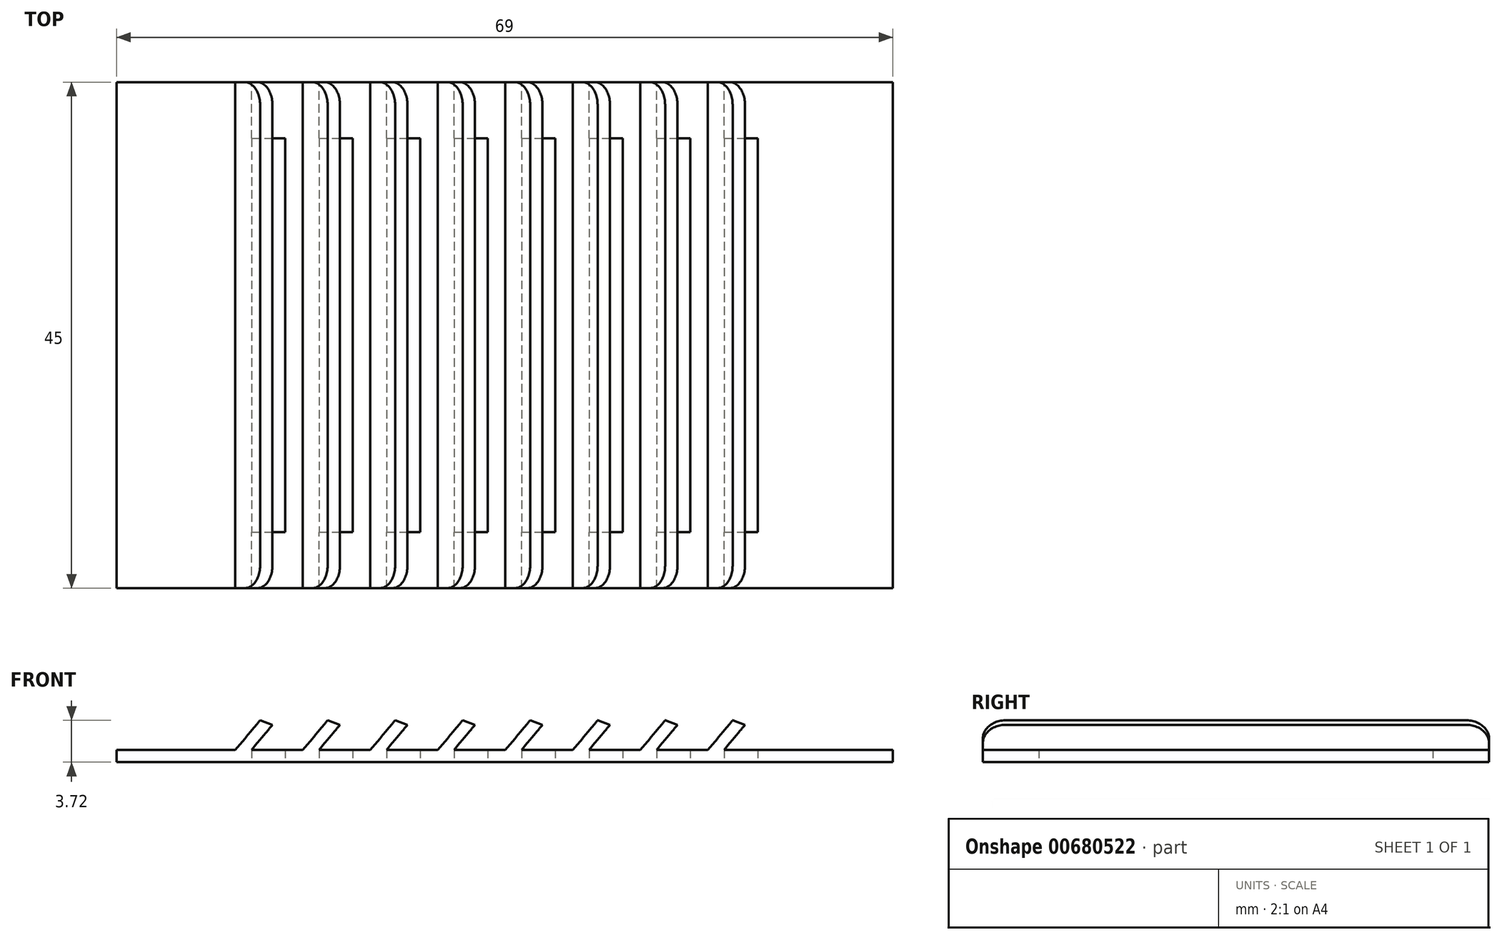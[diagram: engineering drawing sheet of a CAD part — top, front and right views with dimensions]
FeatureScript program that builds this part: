
annotation { "Feature Type Name" : "Feature", "Feature Type Description" : "" }
export const myFeature = defineFeature(function(context is Context, id is Id, definition is map)
    precondition{}
    {
        {
            var Q0;
            Q0=qCreatedBy(makeId("Top.planeOp"),FACE);
            var sketch = newSketch(context, id + "F0", { "sketchPlane" : qUnion([Q0])});
            skLineSegment(sketch, "E0.bottom", {"start": v(0, 0) * mm, "end": v(69, 0) * mm});
            skLineSegment(sketch, "E0.top", {"start": v(0, -45) * mm, "end": v(69, -45) * mm});
            skLineSegment(sketch, "E0.left", {"start": v(0, 0) * mm, "end": v(0, -45) * mm});
            skLineSegment(sketch, "E0.right", {"start": v(69, 0) * mm, "end": v(69, -45) * mm});
            skLineSegment(sketch, "E1.bottom", {"start": v(12, -5) * mm, "end": v(15, -5) * mm});
            skLineSegment(sketch, "E1.top", {"start": v(12, -40) * mm, "end": v(15, -40) * mm});
            skLineSegment(sketch, "E1.left", {"start": v(12, -5) * mm, "end": v(12, -40) * mm});
            skLineSegment(sketch, "E1.right", {"start": v(15, -5) * mm, "end": v(15, -40) * mm});
            skLineSegment(sketch, "E2.1.0.0", {"start": v(18, -40) * mm, "end": v(21, -40) * mm});
            skLineSegment(sketch, "E2.1.0.1", {"start": v(18, -5) * mm, "end": v(21, -5) * mm});
            skLineSegment(sketch, "E2.1.0.2", {"start": v(18, -5) * mm, "end": v(18, -40) * mm});
            skLineSegment(sketch, "E2.1.0.3", {"start": v(21, -5) * mm, "end": v(21, -40) * mm});
            skLineSegment(sketch, "E2.2.0.0", {"start": v(24, -40) * mm, "end": v(27, -40) * mm});
            skLineSegment(sketch, "E2.2.0.1", {"start": v(24, -5) * mm, "end": v(27, -5) * mm});
            skLineSegment(sketch, "E2.2.0.2", {"start": v(24, -5) * mm, "end": v(24, -40) * mm});
            skLineSegment(sketch, "E2.2.0.3", {"start": v(27, -5) * mm, "end": v(27, -40) * mm});
            skLineSegment(sketch, "E2.direction1", {"start": v(12, -40) * mm, "end": v(18, -40) * mm, "construction": true});
            skLineSegment(sketch, "E3.0.3.0", {"start": v(30, -40) * mm, "end": v(33, -40) * mm});
            skLineSegment(sketch, "E3.3.3.0", {"start": v(30, -5) * mm, "end": v(33, -5) * mm});
            skLineSegment(sketch, "E3.6.3.0", {"start": v(30, -5) * mm, "end": v(30, -40) * mm});
            skLineSegment(sketch, "E3.9.3.0", {"start": v(33, -5) * mm, "end": v(33, -40) * mm});
            skLineSegment(sketch, "E3.0.4.0", {"start": v(36, -40) * mm, "end": v(39, -40) * mm});
            skLineSegment(sketch, "E3.3.4.0", {"start": v(36, -5) * mm, "end": v(39, -5) * mm});
            skLineSegment(sketch, "E3.6.4.0", {"start": v(36, -5) * mm, "end": v(36, -40) * mm});
            skLineSegment(sketch, "E3.9.4.0", {"start": v(39, -5) * mm, "end": v(39, -40) * mm});
            skLineSegment(sketch, "E3.0.5.0", {"start": v(42, -40) * mm, "end": v(45, -40) * mm});
            skLineSegment(sketch, "E3.3.5.0", {"start": v(42, -5) * mm, "end": v(45, -5) * mm});
            skLineSegment(sketch, "E3.6.5.0", {"start": v(42, -5) * mm, "end": v(42, -40) * mm});
            skLineSegment(sketch, "E3.9.5.0", {"start": v(45, -5) * mm, "end": v(45, -40) * mm});
            skLineSegment(sketch, "E4.0.6.0", {"start": v(48, -40) * mm, "end": v(51, -40) * mm});
            skLineSegment(sketch, "E4.3.6.0", {"start": v(48, -5) * mm, "end": v(51, -5) * mm});
            skLineSegment(sketch, "E4.6.6.0", {"start": v(48, -5) * mm, "end": v(48, -40) * mm});
            skLineSegment(sketch, "E4.9.6.0", {"start": v(51, -5) * mm, "end": v(51, -40) * mm});
            skLineSegment(sketch, "E4.0.7.0", {"start": v(54, -40) * mm, "end": v(57, -40) * mm});
            skLineSegment(sketch, "E4.3.7.0", {"start": v(54, -5) * mm, "end": v(57, -5) * mm});
            skLineSegment(sketch, "E4.6.7.0", {"start": v(54, -5) * mm, "end": v(54, -40) * mm});
            skLineSegment(sketch, "E4.9.7.0", {"start": v(57, -5) * mm, "end": v(57, -40) * mm});
            skSolve(sketch);
        }
        {
            var Q0;
            Q0=makeQuery(id+"F0.imprint","IMPRINT",FACE,{"disambiguationData":[TD([[makeQuery(id+"F0.imprint","IMPRINT",EDGE,{"derivedFrom":sQuery(id+"F0.wireOp",EDGE,"E0.bottom")}),-1.0]])]});
            extrude(context, id + "F1", {"entities" : qUnion([Q0]), "depth" : 1.1 * mm, "offsetDistance" : 25 * mm});
        }
        {
            var Q0;
            Q0=makeQuery(id+"F1.opExtrude","SWEPT_FACE",FACE,{"disambiguationData":[OSD([sQuery(id+"F0.wireOp",EDGE,"E0.bottom")])]});
            var sketch = newSketch(context, id + "F2", { "sketchPlane" : qUnion([Q0])});
            skLineSegment(sketch, "E5.0.0", {"start": v(0, 0) * mm, "end": v(-69, 0) * mm, "construction": true});
            skLineSegment(sketch, "E5.0.1", {"start": v(-69, 0) * mm, "end": v(-69, 1.1) * mm, "construction": true});
            skLineSegment(sketch, "E5.0.2", {"start": v(-69, 1.1) * mm, "end": v(0, 1.1) * mm});
            skLineSegment(sketch, "E5.0.3", {"start": v(0, 1.1) * mm, "end": v(0, 0) * mm, "construction": true});
            skLineSegment(sketch, "E6.0.0", {"start": v(-12, 0) * mm, "end": v(-15, 0) * mm, "construction": true});
            skLineSegment(sketch, "E6.0.1", {"start": v(-15, 0) * mm, "end": v(-15, 1.1) * mm, "construction": true});
            skLineSegment(sketch, "E6.0.2", {"start": v(-15, 1.1) * mm, "end": v(-12, 1.1) * mm, "construction": true});
            skLineSegment(sketch, "E6.0.3", {"start": v(-12, 1.1) * mm, "end": v(-12, 0) * mm, "construction": true});
            skLineSegment(sketch, "E7.0.0", {"start": v(-54, 0) * mm, "end": v(-57, 0) * mm, "construction": true});
            skLineSegment(sketch, "E7.0.1", {"start": v(-57, 0) * mm, "end": v(-57, 1.1) * mm, "construction": true});
            skLineSegment(sketch, "E7.0.2", {"start": v(-57, 1.1) * mm, "end": v(-54, 1.1) * mm, "construction": true});
            skLineSegment(sketch, "E7.0.3", {"start": v(-54, 1.1) * mm, "end": v(-54, 0) * mm, "construction": true});
            skLineSegment(sketch, "E8", {"start": v(-12, 1.1) * mm, "end": v(-14, 3.48) * mm});
            skLineSegment(sketch, "E9", {"start": v(-14, 3.48) * mm, "end": v(-14, 5.2) * mm});
            skLineSegment(sketch, "E10", {"start": v(-14, 5.2) * mm, "end": v(-10.56, 1.1) * mm});
            skLineSegment(sketch, "E11.1.0.0", {"start": v(-20, 3.48) * mm, "end": v(-20, 5.2) * mm});
            skLineSegment(sketch, "E11.1.0.1", {"start": v(-18, 1.1) * mm, "end": v(-20, 3.48) * mm});
            skLineSegment(sketch, "E11.1.0.2", {"start": v(-20, 5.2) * mm, "end": v(-16.56, 1.1) * mm});
            skLineSegment(sketch, "E11.2.0.0", {"start": v(-26, 3.48) * mm, "end": v(-26, 5.2) * mm});
            skLineSegment(sketch, "E11.2.0.1", {"start": v(-24, 1.1) * mm, "end": v(-26, 3.48) * mm});
            skLineSegment(sketch, "E11.2.0.2", {"start": v(-26, 5.2) * mm, "end": v(-22.56, 1.1) * mm});
            skLineSegment(sketch, "E11.3.0.0", {"start": v(-32, 3.48) * mm, "end": v(-32, 5.2) * mm});
            skLineSegment(sketch, "E11.3.0.1", {"start": v(-30, 1.1) * mm, "end": v(-32, 3.48) * mm});
            skLineSegment(sketch, "E11.3.0.2", {"start": v(-32, 5.2) * mm, "end": v(-28.56, 1.1) * mm});
            skLineSegment(sketch, "E11.4.0.0", {"start": v(-38, 3.48) * mm, "end": v(-38, 5.2) * mm});
            skLineSegment(sketch, "E11.4.0.1", {"start": v(-36, 1.1) * mm, "end": v(-38, 3.48) * mm});
            skLineSegment(sketch, "E11.4.0.2", {"start": v(-38, 5.2) * mm, "end": v(-34.56, 1.1) * mm});
            skLineSegment(sketch, "E11.5.0.0", {"start": v(-44, 3.48) * mm, "end": v(-44, 5.2) * mm});
            skLineSegment(sketch, "E11.5.0.1", {"start": v(-42, 1.1) * mm, "end": v(-44, 3.48) * mm});
            skLineSegment(sketch, "E11.5.0.2", {"start": v(-44, 5.2) * mm, "end": v(-40.56, 1.1) * mm});
            skLineSegment(sketch, "E11.6.0.0", {"start": v(-50, 3.48) * mm, "end": v(-50, 5.2) * mm});
            skLineSegment(sketch, "E11.6.0.1", {"start": v(-48, 1.1) * mm, "end": v(-50, 3.48) * mm});
            skLineSegment(sketch, "E11.6.0.2", {"start": v(-50, 5.2) * mm, "end": v(-46.56, 1.1) * mm});
            skLineSegment(sketch, "E11.7.0.0", {"start": v(-56, 3.48) * mm, "end": v(-56, 5.2) * mm});
            skLineSegment(sketch, "E11.7.0.1", {"start": v(-54, 1.1) * mm, "end": v(-56, 3.48) * mm});
            skLineSegment(sketch, "E11.7.0.2", {"start": v(-56, 5.2) * mm, "end": v(-52.56, 1.1) * mm});
            skLineSegment(sketch, "E11.direction1", {"start": v(-14, 3.48) * mm, "end": v(-20, 3.48) * mm, "construction": true});
            skSolve(sketch);
        }
        {
            var Q0;
            {var subQ0=sQuery(id+"F2.wireOp",EDGE,"E8");Q0=makeQuery(id+"F2.imprint","IMPRINT",FACE,{"disambiguationData":[TD([[makeQuery(id+"F2.imprint","IMPRINT",EDGE,{"derivedFrom":subQ0}),-1.0]])]});}
            var Q1;
            Q1=makeQuery(id+"F2.imprint","IMPRINT",FACE,{"disambiguationData":[TD([[makeQuery(id+"F2.imprint","IMPRINT",EDGE,{"derivedFrom":sQuery(id+"F2.wireOp",EDGE,"E11.1.0.0")}),-1.0]])]});
            var Q2;
            Q2=makeQuery(id+"F2.imprint","IMPRINT",FACE,{"disambiguationData":[TD([[makeQuery(id+"F2.imprint","IMPRINT",EDGE,{"derivedFrom":sQuery(id+"F2.wireOp",EDGE,"E11.2.0.0")}),-1.0]])]});
            var Q3;
            Q3=makeQuery(id+"F2.imprint","IMPRINT",FACE,{"disambiguationData":[TD([[makeQuery(id+"F2.imprint","IMPRINT",EDGE,{"derivedFrom":sQuery(id+"F2.wireOp",EDGE,"E11.3.0.0")}),-1.0]])]});
            var Q4;
            Q4=makeQuery(id+"F2.imprint","IMPRINT",FACE,{"disambiguationData":[TD([[makeQuery(id+"F2.imprint","IMPRINT",EDGE,{"derivedFrom":sQuery(id+"F2.wireOp",EDGE,"E11.4.0.0")}),-1.0]])]});
            var Q5;
            Q5=makeQuery(id+"F2.imprint","IMPRINT",FACE,{"disambiguationData":[TD([[makeQuery(id+"F2.imprint","IMPRINT",EDGE,{"derivedFrom":sQuery(id+"F2.wireOp",EDGE,"E11.5.0.0")}),-1.0]])]});
            var Q6;
            Q6=makeQuery(id+"F2.imprint","IMPRINT",FACE,{"disambiguationData":[TD([[makeQuery(id+"F2.imprint","IMPRINT",EDGE,{"derivedFrom":sQuery(id+"F2.wireOp",EDGE,"E11.6.0.0")}),-1.0]])]});
            var Q7;
            Q7=makeQuery(id+"F2.imprint","IMPRINT",FACE,{"disambiguationData":[TD([[makeQuery(id+"F2.imprint","IMPRINT",EDGE,{"derivedFrom":sQuery(id+"F2.wireOp",EDGE,"E11.7.0.0")}),-1.0]])]});
            var Q8;
            Q8=makeQuery(id+"F1.opExtrude","SWEPT_FACE",FACE,{"disambiguationData":[OSD([sQuery(id+"F0.wireOp",EDGE,"E0.top")])]});
            extrude(context, id + "F3", {"entities" : qUnion([Q0, Q1, Q2, Q3, Q4, Q5, Q6, Q7]), "operationType" : NewBodyOperationType.ADD, "endBound" : BoundingType.UP_TO_SURFACE, "oppositeDirection" : true, "depth" : 25 * mm, "endBoundEntityFace" : qUnion([Q8]), "offsetDistance" : 25 * mm});
        }
        {
            var Q0;
            Q0=makeQuery(id+"F3.opExtrude","SWEPT_EDGE",EDGE,{"disambiguationData":[OSD([sQuery(id+"F2.wireOp",EDGE,"E9"),sQuery(id+"F2.wireOp",EDGE,"E10")])]});
            var Q1;
            Q1=makeQuery(id+"F3.opExtrude","SWEPT_EDGE",EDGE,{"disambiguationData":[OSD([sQuery(id+"F2.wireOp",EDGE,"E11.1.0.0"),sQuery(id+"F2.wireOp",EDGE,"E11.1.0.2")])]});
            var Q2;
            Q2=makeQuery(id+"F3.opExtrude","SWEPT_EDGE",EDGE,{"disambiguationData":[OSD([sQuery(id+"F2.wireOp",EDGE,"E11.2.0.0"),sQuery(id+"F2.wireOp",EDGE,"E11.2.0.2")])]});
            var Q3;
            Q3=makeQuery(id+"F3.opExtrude","SWEPT_EDGE",EDGE,{"disambiguationData":[OSD([sQuery(id+"F2.wireOp",EDGE,"E11.3.0.0"),sQuery(id+"F2.wireOp",EDGE,"E11.3.0.2")])]});
            var Q4;
            Q4=makeQuery(id+"F3.opExtrude","SWEPT_EDGE",EDGE,{"disambiguationData":[OSD([sQuery(id+"F2.wireOp",EDGE,"E11.4.0.0"),sQuery(id+"F2.wireOp",EDGE,"E11.4.0.2")])]});
            var Q5;
            Q5=makeQuery(id+"F3.opExtrude","SWEPT_EDGE",EDGE,{"disambiguationData":[OSD([sQuery(id+"F2.wireOp",EDGE,"E11.5.0.0"),sQuery(id+"F2.wireOp",EDGE,"E11.5.0.2")])]});
            var Q6;
            Q6=makeQuery(id+"F3.opExtrude","SWEPT_EDGE",EDGE,{"disambiguationData":[OSD([sQuery(id+"F2.wireOp",EDGE,"E11.6.0.0"),sQuery(id+"F2.wireOp",EDGE,"E11.6.0.2")])]});
            var Q7;
            Q7=makeQuery(id+"F3.opExtrude","SWEPT_EDGE",EDGE,{"disambiguationData":[OSD([sQuery(id+"F2.wireOp",EDGE,"E11.7.0.0"),sQuery(id+"F2.wireOp",EDGE,"E11.7.0.2")])]});
            chamfer(context, id + "F4", {"entities" : qUnion([Q0, Q1, Q2, Q3, Q4, Q5, Q6, Q7]), "width" : .7 * mm, "tangentPropagation" : true});
        }
        {
            var Q0;
            {var subQ0=sQuery(id+"F0.wireOp",EDGE,"E0.top");Q0=makeQuery(id+"F4.opChamfer","BLEND_EDGE",EDGE,{"blendedFrom":[makeQuery(id+"F3.opExtrude","SWEPT_EDGE",EDGE,{"disambiguationData":[OSD([sQuery(id+"F2.wireOp",EDGE,"E11.2.0.0"),sQuery(id+"F2.wireOp",EDGE,"E11.2.0.2")])]}),makeQuery(id+"F3.boolean.opBoolean","MERGE",FACE,{"derivedFrom":[makeQuery(id+"F1.opExtrude","SWEPT_FACE",FACE,{"disambiguationData":[OSD([subQ0])]}),makeQuery(id+"F3.opExtrude","CAP_FACE",FACE,{"disambiguationData":[OSD([subQ0]),OD(0.0)],"isStart":false}),makeQuery(id+"F3.opExtrude","CAP_FACE",FACE,{"disambiguationData":[OSD([subQ0]),OD(1.0)],"isStart":false}),makeQuery(id+"F3.opExtrude","CAP_FACE",FACE,{"disambiguationData":[OSD([subQ0]),OD(2.0)],"isStart":false}),makeQuery(id+"F3.opExtrude","CAP_FACE",FACE,{"disambiguationData":[OSD([subQ0]),OD(3.0)],"isStart":false}),makeQuery(id+"F3.opExtrude","CAP_FACE",FACE,{"disambiguationData":[OSD([subQ0]),OD(4.0)],"isStart":false}),makeQuery(id+"F3.opExtrude","CAP_FACE",FACE,{"disambiguationData":[OSD([subQ0]),OD(5.0)],"isStart":false}),makeQuery(id+"F3.opExtrude","CAP_FACE",FACE,{"disambiguationData":[OSD([subQ0]),OD(6.0)],"isStart":false}),makeQuery(id+"F3.opExtrude","CAP_FACE",FACE,{"disambiguationData":[OSD([subQ0]),OD(7.0)],"isStart":false})]})],"blendedInto":[makeQuery(id+"F3.boolean.opBoolean","MERGE",FACE,{"derivedFrom":[makeQuery(id+"F1.opExtrude","SWEPT_FACE",FACE,{"disambiguationData":[OSD([subQ0])]}),makeQuery(id+"F3.opExtrude","CAP_FACE",FACE,{"disambiguationData":[OSD([subQ0]),OD(0.0)],"isStart":false}),makeQuery(id+"F3.opExtrude","CAP_FACE",FACE,{"disambiguationData":[OSD([subQ0]),OD(1.0)],"isStart":false}),makeQuery(id+"F3.opExtrude","CAP_FACE",FACE,{"disambiguationData":[OSD([subQ0]),OD(2.0)],"isStart":false}),makeQuery(id+"F3.opExtrude","CAP_FACE",FACE,{"disambiguationData":[OSD([subQ0]),OD(3.0)],"isStart":false}),makeQuery(id+"F3.opExtrude","CAP_FACE",FACE,{"disambiguationData":[OSD([subQ0]),OD(4.0)],"isStart":false}),makeQuery(id+"F3.opExtrude","CAP_FACE",FACE,{"disambiguationData":[OSD([subQ0]),OD(5.0)],"isStart":false}),makeQuery(id+"F3.opExtrude","CAP_FACE",FACE,{"disambiguationData":[OSD([subQ0]),OD(6.0)],"isStart":false}),makeQuery(id+"F3.opExtrude","CAP_FACE",FACE,{"disambiguationData":[OSD([subQ0]),OD(7.0)],"isStart":false})]})]});}
            var Q1;
            {var subQ0=sQuery(id+"F0.wireOp",EDGE,"E0.top");Q1=makeQuery(id+"F4.opChamfer","BLEND_EDGE",EDGE,{"blendedFrom":[makeQuery(id+"F3.opExtrude","SWEPT_EDGE",EDGE,{"disambiguationData":[OSD([sQuery(id+"F2.wireOp",EDGE,"E9"),sQuery(id+"F2.wireOp",EDGE,"E10")])]}),makeQuery(id+"F3.boolean.opBoolean","MERGE",FACE,{"derivedFrom":[makeQuery(id+"F1.opExtrude","SWEPT_FACE",FACE,{"disambiguationData":[OSD([subQ0])]}),makeQuery(id+"F3.opExtrude","CAP_FACE",FACE,{"disambiguationData":[OSD([subQ0]),OD(0.0)],"isStart":false}),makeQuery(id+"F3.opExtrude","CAP_FACE",FACE,{"disambiguationData":[OSD([subQ0]),OD(1.0)],"isStart":false}),makeQuery(id+"F3.opExtrude","CAP_FACE",FACE,{"disambiguationData":[OSD([subQ0]),OD(2.0)],"isStart":false}),makeQuery(id+"F3.opExtrude","CAP_FACE",FACE,{"disambiguationData":[OSD([subQ0]),OD(3.0)],"isStart":false}),makeQuery(id+"F3.opExtrude","CAP_FACE",FACE,{"disambiguationData":[OSD([subQ0]),OD(4.0)],"isStart":false}),makeQuery(id+"F3.opExtrude","CAP_FACE",FACE,{"disambiguationData":[OSD([subQ0]),OD(5.0)],"isStart":false}),makeQuery(id+"F3.opExtrude","CAP_FACE",FACE,{"disambiguationData":[OSD([subQ0]),OD(6.0)],"isStart":false}),makeQuery(id+"F3.opExtrude","CAP_FACE",FACE,{"disambiguationData":[OSD([subQ0]),OD(7.0)],"isStart":false})]})],"blendedInto":[makeQuery(id+"F3.boolean.opBoolean","MERGE",FACE,{"derivedFrom":[makeQuery(id+"F1.opExtrude","SWEPT_FACE",FACE,{"disambiguationData":[OSD([subQ0])]}),makeQuery(id+"F3.opExtrude","CAP_FACE",FACE,{"disambiguationData":[OSD([subQ0]),OD(0.0)],"isStart":false}),makeQuery(id+"F3.opExtrude","CAP_FACE",FACE,{"disambiguationData":[OSD([subQ0]),OD(1.0)],"isStart":false}),makeQuery(id+"F3.opExtrude","CAP_FACE",FACE,{"disambiguationData":[OSD([subQ0]),OD(2.0)],"isStart":false}),makeQuery(id+"F3.opExtrude","CAP_FACE",FACE,{"disambiguationData":[OSD([subQ0]),OD(3.0)],"isStart":false}),makeQuery(id+"F3.opExtrude","CAP_FACE",FACE,{"disambiguationData":[OSD([subQ0]),OD(4.0)],"isStart":false}),makeQuery(id+"F3.opExtrude","CAP_FACE",FACE,{"disambiguationData":[OSD([subQ0]),OD(5.0)],"isStart":false}),makeQuery(id+"F3.opExtrude","CAP_FACE",FACE,{"disambiguationData":[OSD([subQ0]),OD(6.0)],"isStart":false}),makeQuery(id+"F3.opExtrude","CAP_FACE",FACE,{"disambiguationData":[OSD([subQ0]),OD(7.0)],"isStart":false})]})]});}
            var Q2;
            {var subQ0=sQuery(id+"F0.wireOp",EDGE,"E0.top");Q2=makeQuery(id+"F4.opChamfer","BLEND_EDGE",EDGE,{"blendedFrom":[makeQuery(id+"F3.opExtrude","SWEPT_EDGE",EDGE,{"disambiguationData":[OSD([sQuery(id+"F2.wireOp",EDGE,"E11.1.0.0"),sQuery(id+"F2.wireOp",EDGE,"E11.1.0.2")])]}),makeQuery(id+"F3.boolean.opBoolean","MERGE",FACE,{"derivedFrom":[makeQuery(id+"F1.opExtrude","SWEPT_FACE",FACE,{"disambiguationData":[OSD([subQ0])]}),makeQuery(id+"F3.opExtrude","CAP_FACE",FACE,{"disambiguationData":[OSD([subQ0]),OD(0.0)],"isStart":false}),makeQuery(id+"F3.opExtrude","CAP_FACE",FACE,{"disambiguationData":[OSD([subQ0]),OD(1.0)],"isStart":false}),makeQuery(id+"F3.opExtrude","CAP_FACE",FACE,{"disambiguationData":[OSD([subQ0]),OD(2.0)],"isStart":false}),makeQuery(id+"F3.opExtrude","CAP_FACE",FACE,{"disambiguationData":[OSD([subQ0]),OD(3.0)],"isStart":false}),makeQuery(id+"F3.opExtrude","CAP_FACE",FACE,{"disambiguationData":[OSD([subQ0]),OD(4.0)],"isStart":false}),makeQuery(id+"F3.opExtrude","CAP_FACE",FACE,{"disambiguationData":[OSD([subQ0]),OD(5.0)],"isStart":false}),makeQuery(id+"F3.opExtrude","CAP_FACE",FACE,{"disambiguationData":[OSD([subQ0]),OD(6.0)],"isStart":false}),makeQuery(id+"F3.opExtrude","CAP_FACE",FACE,{"disambiguationData":[OSD([subQ0]),OD(7.0)],"isStart":false})]})],"blendedInto":[makeQuery(id+"F3.boolean.opBoolean","MERGE",FACE,{"derivedFrom":[makeQuery(id+"F1.opExtrude","SWEPT_FACE",FACE,{"disambiguationData":[OSD([subQ0])]}),makeQuery(id+"F3.opExtrude","CAP_FACE",FACE,{"disambiguationData":[OSD([subQ0]),OD(0.0)],"isStart":false}),makeQuery(id+"F3.opExtrude","CAP_FACE",FACE,{"disambiguationData":[OSD([subQ0]),OD(1.0)],"isStart":false}),makeQuery(id+"F3.opExtrude","CAP_FACE",FACE,{"disambiguationData":[OSD([subQ0]),OD(2.0)],"isStart":false}),makeQuery(id+"F3.opExtrude","CAP_FACE",FACE,{"disambiguationData":[OSD([subQ0]),OD(3.0)],"isStart":false}),makeQuery(id+"F3.opExtrude","CAP_FACE",FACE,{"disambiguationData":[OSD([subQ0]),OD(4.0)],"isStart":false}),makeQuery(id+"F3.opExtrude","CAP_FACE",FACE,{"disambiguationData":[OSD([subQ0]),OD(5.0)],"isStart":false}),makeQuery(id+"F3.opExtrude","CAP_FACE",FACE,{"disambiguationData":[OSD([subQ0]),OD(6.0)],"isStart":false}),makeQuery(id+"F3.opExtrude","CAP_FACE",FACE,{"disambiguationData":[OSD([subQ0]),OD(7.0)],"isStart":false})]})]});}
            var Q3;
            {var subQ0=sQuery(id+"F0.wireOp",EDGE,"E0.top");Q3=makeQuery(id+"F4.opChamfer","BLEND_EDGE",EDGE,{"blendedFrom":[makeQuery(id+"F3.opExtrude","SWEPT_EDGE",EDGE,{"disambiguationData":[OSD([sQuery(id+"F2.wireOp",EDGE,"E11.3.0.0"),sQuery(id+"F2.wireOp",EDGE,"E11.3.0.2")])]}),makeQuery(id+"F3.boolean.opBoolean","MERGE",FACE,{"derivedFrom":[makeQuery(id+"F1.opExtrude","SWEPT_FACE",FACE,{"disambiguationData":[OSD([subQ0])]}),makeQuery(id+"F3.opExtrude","CAP_FACE",FACE,{"disambiguationData":[OSD([subQ0]),OD(0.0)],"isStart":false}),makeQuery(id+"F3.opExtrude","CAP_FACE",FACE,{"disambiguationData":[OSD([subQ0]),OD(1.0)],"isStart":false}),makeQuery(id+"F3.opExtrude","CAP_FACE",FACE,{"disambiguationData":[OSD([subQ0]),OD(2.0)],"isStart":false}),makeQuery(id+"F3.opExtrude","CAP_FACE",FACE,{"disambiguationData":[OSD([subQ0]),OD(3.0)],"isStart":false}),makeQuery(id+"F3.opExtrude","CAP_FACE",FACE,{"disambiguationData":[OSD([subQ0]),OD(4.0)],"isStart":false}),makeQuery(id+"F3.opExtrude","CAP_FACE",FACE,{"disambiguationData":[OSD([subQ0]),OD(5.0)],"isStart":false}),makeQuery(id+"F3.opExtrude","CAP_FACE",FACE,{"disambiguationData":[OSD([subQ0]),OD(6.0)],"isStart":false}),makeQuery(id+"F3.opExtrude","CAP_FACE",FACE,{"disambiguationData":[OSD([subQ0]),OD(7.0)],"isStart":false})]})],"blendedInto":[makeQuery(id+"F3.boolean.opBoolean","MERGE",FACE,{"derivedFrom":[makeQuery(id+"F1.opExtrude","SWEPT_FACE",FACE,{"disambiguationData":[OSD([subQ0])]}),makeQuery(id+"F3.opExtrude","CAP_FACE",FACE,{"disambiguationData":[OSD([subQ0]),OD(0.0)],"isStart":false}),makeQuery(id+"F3.opExtrude","CAP_FACE",FACE,{"disambiguationData":[OSD([subQ0]),OD(1.0)],"isStart":false}),makeQuery(id+"F3.opExtrude","CAP_FACE",FACE,{"disambiguationData":[OSD([subQ0]),OD(2.0)],"isStart":false}),makeQuery(id+"F3.opExtrude","CAP_FACE",FACE,{"disambiguationData":[OSD([subQ0]),OD(3.0)],"isStart":false}),makeQuery(id+"F3.opExtrude","CAP_FACE",FACE,{"disambiguationData":[OSD([subQ0]),OD(4.0)],"isStart":false}),makeQuery(id+"F3.opExtrude","CAP_FACE",FACE,{"disambiguationData":[OSD([subQ0]),OD(5.0)],"isStart":false}),makeQuery(id+"F3.opExtrude","CAP_FACE",FACE,{"disambiguationData":[OSD([subQ0]),OD(6.0)],"isStart":false}),makeQuery(id+"F3.opExtrude","CAP_FACE",FACE,{"disambiguationData":[OSD([subQ0]),OD(7.0)],"isStart":false})]})]});}
            var Q4;
            {var subQ0=sQuery(id+"F0.wireOp",EDGE,"E0.top");Q4=makeQuery(id+"F4.opChamfer","BLEND_EDGE",EDGE,{"blendedFrom":[makeQuery(id+"F3.opExtrude","SWEPT_EDGE",EDGE,{"disambiguationData":[OSD([sQuery(id+"F2.wireOp",EDGE,"E11.4.0.0"),sQuery(id+"F2.wireOp",EDGE,"E11.4.0.2")])]}),makeQuery(id+"F3.boolean.opBoolean","MERGE",FACE,{"derivedFrom":[makeQuery(id+"F1.opExtrude","SWEPT_FACE",FACE,{"disambiguationData":[OSD([subQ0])]}),makeQuery(id+"F3.opExtrude","CAP_FACE",FACE,{"disambiguationData":[OSD([subQ0]),OD(0.0)],"isStart":false}),makeQuery(id+"F3.opExtrude","CAP_FACE",FACE,{"disambiguationData":[OSD([subQ0]),OD(1.0)],"isStart":false}),makeQuery(id+"F3.opExtrude","CAP_FACE",FACE,{"disambiguationData":[OSD([subQ0]),OD(2.0)],"isStart":false}),makeQuery(id+"F3.opExtrude","CAP_FACE",FACE,{"disambiguationData":[OSD([subQ0]),OD(3.0)],"isStart":false}),makeQuery(id+"F3.opExtrude","CAP_FACE",FACE,{"disambiguationData":[OSD([subQ0]),OD(4.0)],"isStart":false}),makeQuery(id+"F3.opExtrude","CAP_FACE",FACE,{"disambiguationData":[OSD([subQ0]),OD(5.0)],"isStart":false}),makeQuery(id+"F3.opExtrude","CAP_FACE",FACE,{"disambiguationData":[OSD([subQ0]),OD(6.0)],"isStart":false}),makeQuery(id+"F3.opExtrude","CAP_FACE",FACE,{"disambiguationData":[OSD([subQ0]),OD(7.0)],"isStart":false})]})],"blendedInto":[makeQuery(id+"F3.boolean.opBoolean","MERGE",FACE,{"derivedFrom":[makeQuery(id+"F1.opExtrude","SWEPT_FACE",FACE,{"disambiguationData":[OSD([subQ0])]}),makeQuery(id+"F3.opExtrude","CAP_FACE",FACE,{"disambiguationData":[OSD([subQ0]),OD(0.0)],"isStart":false}),makeQuery(id+"F3.opExtrude","CAP_FACE",FACE,{"disambiguationData":[OSD([subQ0]),OD(1.0)],"isStart":false}),makeQuery(id+"F3.opExtrude","CAP_FACE",FACE,{"disambiguationData":[OSD([subQ0]),OD(2.0)],"isStart":false}),makeQuery(id+"F3.opExtrude","CAP_FACE",FACE,{"disambiguationData":[OSD([subQ0]),OD(3.0)],"isStart":false}),makeQuery(id+"F3.opExtrude","CAP_FACE",FACE,{"disambiguationData":[OSD([subQ0]),OD(4.0)],"isStart":false}),makeQuery(id+"F3.opExtrude","CAP_FACE",FACE,{"disambiguationData":[OSD([subQ0]),OD(5.0)],"isStart":false}),makeQuery(id+"F3.opExtrude","CAP_FACE",FACE,{"disambiguationData":[OSD([subQ0]),OD(6.0)],"isStart":false}),makeQuery(id+"F3.opExtrude","CAP_FACE",FACE,{"disambiguationData":[OSD([subQ0]),OD(7.0)],"isStart":false})]})]});}
            var Q5;
            {var subQ0=sQuery(id+"F0.wireOp",EDGE,"E0.top");Q5=makeQuery(id+"F4.opChamfer","BLEND_EDGE",EDGE,{"blendedFrom":[makeQuery(id+"F3.opExtrude","SWEPT_EDGE",EDGE,{"disambiguationData":[OSD([sQuery(id+"F2.wireOp",EDGE,"E11.5.0.0"),sQuery(id+"F2.wireOp",EDGE,"E11.5.0.2")])]}),makeQuery(id+"F3.boolean.opBoolean","MERGE",FACE,{"derivedFrom":[makeQuery(id+"F1.opExtrude","SWEPT_FACE",FACE,{"disambiguationData":[OSD([subQ0])]}),makeQuery(id+"F3.opExtrude","CAP_FACE",FACE,{"disambiguationData":[OSD([subQ0]),OD(0.0)],"isStart":false}),makeQuery(id+"F3.opExtrude","CAP_FACE",FACE,{"disambiguationData":[OSD([subQ0]),OD(1.0)],"isStart":false}),makeQuery(id+"F3.opExtrude","CAP_FACE",FACE,{"disambiguationData":[OSD([subQ0]),OD(2.0)],"isStart":false}),makeQuery(id+"F3.opExtrude","CAP_FACE",FACE,{"disambiguationData":[OSD([subQ0]),OD(3.0)],"isStart":false}),makeQuery(id+"F3.opExtrude","CAP_FACE",FACE,{"disambiguationData":[OSD([subQ0]),OD(4.0)],"isStart":false}),makeQuery(id+"F3.opExtrude","CAP_FACE",FACE,{"disambiguationData":[OSD([subQ0]),OD(5.0)],"isStart":false}),makeQuery(id+"F3.opExtrude","CAP_FACE",FACE,{"disambiguationData":[OSD([subQ0]),OD(6.0)],"isStart":false}),makeQuery(id+"F3.opExtrude","CAP_FACE",FACE,{"disambiguationData":[OSD([subQ0]),OD(7.0)],"isStart":false})]})],"blendedInto":[makeQuery(id+"F3.boolean.opBoolean","MERGE",FACE,{"derivedFrom":[makeQuery(id+"F1.opExtrude","SWEPT_FACE",FACE,{"disambiguationData":[OSD([subQ0])]}),makeQuery(id+"F3.opExtrude","CAP_FACE",FACE,{"disambiguationData":[OSD([subQ0]),OD(0.0)],"isStart":false}),makeQuery(id+"F3.opExtrude","CAP_FACE",FACE,{"disambiguationData":[OSD([subQ0]),OD(1.0)],"isStart":false}),makeQuery(id+"F3.opExtrude","CAP_FACE",FACE,{"disambiguationData":[OSD([subQ0]),OD(2.0)],"isStart":false}),makeQuery(id+"F3.opExtrude","CAP_FACE",FACE,{"disambiguationData":[OSD([subQ0]),OD(3.0)],"isStart":false}),makeQuery(id+"F3.opExtrude","CAP_FACE",FACE,{"disambiguationData":[OSD([subQ0]),OD(4.0)],"isStart":false}),makeQuery(id+"F3.opExtrude","CAP_FACE",FACE,{"disambiguationData":[OSD([subQ0]),OD(5.0)],"isStart":false}),makeQuery(id+"F3.opExtrude","CAP_FACE",FACE,{"disambiguationData":[OSD([subQ0]),OD(6.0)],"isStart":false}),makeQuery(id+"F3.opExtrude","CAP_FACE",FACE,{"disambiguationData":[OSD([subQ0]),OD(7.0)],"isStart":false})]})]});}
            var Q6;
            {var subQ0=sQuery(id+"F0.wireOp",EDGE,"E0.top");Q6=makeQuery(id+"F4.opChamfer","BLEND_EDGE",EDGE,{"blendedFrom":[makeQuery(id+"F3.opExtrude","SWEPT_EDGE",EDGE,{"disambiguationData":[OSD([sQuery(id+"F2.wireOp",EDGE,"E11.6.0.0"),sQuery(id+"F2.wireOp",EDGE,"E11.6.0.2")])]}),makeQuery(id+"F3.boolean.opBoolean","MERGE",FACE,{"derivedFrom":[makeQuery(id+"F1.opExtrude","SWEPT_FACE",FACE,{"disambiguationData":[OSD([subQ0])]}),makeQuery(id+"F3.opExtrude","CAP_FACE",FACE,{"disambiguationData":[OSD([subQ0]),OD(0.0)],"isStart":false}),makeQuery(id+"F3.opExtrude","CAP_FACE",FACE,{"disambiguationData":[OSD([subQ0]),OD(1.0)],"isStart":false}),makeQuery(id+"F3.opExtrude","CAP_FACE",FACE,{"disambiguationData":[OSD([subQ0]),OD(2.0)],"isStart":false}),makeQuery(id+"F3.opExtrude","CAP_FACE",FACE,{"disambiguationData":[OSD([subQ0]),OD(3.0)],"isStart":false}),makeQuery(id+"F3.opExtrude","CAP_FACE",FACE,{"disambiguationData":[OSD([subQ0]),OD(4.0)],"isStart":false}),makeQuery(id+"F3.opExtrude","CAP_FACE",FACE,{"disambiguationData":[OSD([subQ0]),OD(5.0)],"isStart":false}),makeQuery(id+"F3.opExtrude","CAP_FACE",FACE,{"disambiguationData":[OSD([subQ0]),OD(6.0)],"isStart":false}),makeQuery(id+"F3.opExtrude","CAP_FACE",FACE,{"disambiguationData":[OSD([subQ0]),OD(7.0)],"isStart":false})]})],"blendedInto":[makeQuery(id+"F3.boolean.opBoolean","MERGE",FACE,{"derivedFrom":[makeQuery(id+"F1.opExtrude","SWEPT_FACE",FACE,{"disambiguationData":[OSD([subQ0])]}),makeQuery(id+"F3.opExtrude","CAP_FACE",FACE,{"disambiguationData":[OSD([subQ0]),OD(0.0)],"isStart":false}),makeQuery(id+"F3.opExtrude","CAP_FACE",FACE,{"disambiguationData":[OSD([subQ0]),OD(1.0)],"isStart":false}),makeQuery(id+"F3.opExtrude","CAP_FACE",FACE,{"disambiguationData":[OSD([subQ0]),OD(2.0)],"isStart":false}),makeQuery(id+"F3.opExtrude","CAP_FACE",FACE,{"disambiguationData":[OSD([subQ0]),OD(3.0)],"isStart":false}),makeQuery(id+"F3.opExtrude","CAP_FACE",FACE,{"disambiguationData":[OSD([subQ0]),OD(4.0)],"isStart":false}),makeQuery(id+"F3.opExtrude","CAP_FACE",FACE,{"disambiguationData":[OSD([subQ0]),OD(5.0)],"isStart":false}),makeQuery(id+"F3.opExtrude","CAP_FACE",FACE,{"disambiguationData":[OSD([subQ0]),OD(6.0)],"isStart":false}),makeQuery(id+"F3.opExtrude","CAP_FACE",FACE,{"disambiguationData":[OSD([subQ0]),OD(7.0)],"isStart":false})]})]});}
            var Q7;
            {var subQ0=sQuery(id+"F0.wireOp",EDGE,"E0.top");Q7=makeQuery(id+"F4.opChamfer","BLEND_EDGE",EDGE,{"blendedFrom":[makeQuery(id+"F3.opExtrude","SWEPT_EDGE",EDGE,{"disambiguationData":[OSD([sQuery(id+"F2.wireOp",EDGE,"E11.7.0.0"),sQuery(id+"F2.wireOp",EDGE,"E11.7.0.2")])]}),makeQuery(id+"F3.boolean.opBoolean","MERGE",FACE,{"derivedFrom":[makeQuery(id+"F1.opExtrude","SWEPT_FACE",FACE,{"disambiguationData":[OSD([subQ0])]}),makeQuery(id+"F3.opExtrude","CAP_FACE",FACE,{"disambiguationData":[OSD([subQ0]),OD(0.0)],"isStart":false}),makeQuery(id+"F3.opExtrude","CAP_FACE",FACE,{"disambiguationData":[OSD([subQ0]),OD(1.0)],"isStart":false}),makeQuery(id+"F3.opExtrude","CAP_FACE",FACE,{"disambiguationData":[OSD([subQ0]),OD(2.0)],"isStart":false}),makeQuery(id+"F3.opExtrude","CAP_FACE",FACE,{"disambiguationData":[OSD([subQ0]),OD(3.0)],"isStart":false}),makeQuery(id+"F3.opExtrude","CAP_FACE",FACE,{"disambiguationData":[OSD([subQ0]),OD(4.0)],"isStart":false}),makeQuery(id+"F3.opExtrude","CAP_FACE",FACE,{"disambiguationData":[OSD([subQ0]),OD(5.0)],"isStart":false}),makeQuery(id+"F3.opExtrude","CAP_FACE",FACE,{"disambiguationData":[OSD([subQ0]),OD(6.0)],"isStart":false}),makeQuery(id+"F3.opExtrude","CAP_FACE",FACE,{"disambiguationData":[OSD([subQ0]),OD(7.0)],"isStart":false})]})],"blendedInto":[makeQuery(id+"F3.boolean.opBoolean","MERGE",FACE,{"derivedFrom":[makeQuery(id+"F1.opExtrude","SWEPT_FACE",FACE,{"disambiguationData":[OSD([subQ0])]}),makeQuery(id+"F3.opExtrude","CAP_FACE",FACE,{"disambiguationData":[OSD([subQ0]),OD(0.0)],"isStart":false}),makeQuery(id+"F3.opExtrude","CAP_FACE",FACE,{"disambiguationData":[OSD([subQ0]),OD(1.0)],"isStart":false}),makeQuery(id+"F3.opExtrude","CAP_FACE",FACE,{"disambiguationData":[OSD([subQ0]),OD(2.0)],"isStart":false}),makeQuery(id+"F3.opExtrude","CAP_FACE",FACE,{"disambiguationData":[OSD([subQ0]),OD(3.0)],"isStart":false}),makeQuery(id+"F3.opExtrude","CAP_FACE",FACE,{"disambiguationData":[OSD([subQ0]),OD(4.0)],"isStart":false}),makeQuery(id+"F3.opExtrude","CAP_FACE",FACE,{"disambiguationData":[OSD([subQ0]),OD(5.0)],"isStart":false}),makeQuery(id+"F3.opExtrude","CAP_FACE",FACE,{"disambiguationData":[OSD([subQ0]),OD(6.0)],"isStart":false}),makeQuery(id+"F3.opExtrude","CAP_FACE",FACE,{"disambiguationData":[OSD([subQ0]),OD(7.0)],"isStart":false})]})]});}
            var Q8;
            {var subQ0=sQuery(id+"F2.wireOp",EDGE,"E5.0.2");var subQ1=sQuery(id+"F2.wireOp",EDGE,"E10");var subQ2=sQuery(id+"F2.wireOp",EDGE,"E9");Q8=makeQuery(id+"F4.opChamfer","BLEND_EDGE",EDGE,{"blendedFrom":[makeQuery(id+"F3.opExtrude","SWEPT_EDGE",EDGE,{"disambiguationData":[OSD([subQ2,subQ1])]}),makeQuery(id+"F3.boolean.opBoolean","MERGE",FACE,{"derivedFrom":[makeQuery(id+"F1.opExtrude","SWEPT_FACE",FACE,{"disambiguationData":[OSD([sQuery(id+"F0.wireOp",EDGE,"E0.bottom")])]}),makeQuery(id+"F3.opExtrude","CAP_FACE",FACE,{"disambiguationData":[OSD([subQ0,sQuery(id+"F2.wireOp",EDGE,"E8"),subQ2,subQ1])],"isStart":true}),makeQuery(id+"F3.opExtrude","CAP_FACE",FACE,{"disambiguationData":[OSD([subQ0,sQuery(id+"F2.wireOp",EDGE,"E11.1.0.0"),sQuery(id+"F2.wireOp",EDGE,"E11.1.0.1"),sQuery(id+"F2.wireOp",EDGE,"E11.1.0.2")])],"isStart":true}),makeQuery(id+"F3.opExtrude","CAP_FACE",FACE,{"disambiguationData":[OSD([subQ0,sQuery(id+"F2.wireOp",EDGE,"E11.2.0.0"),sQuery(id+"F2.wireOp",EDGE,"E11.2.0.1"),sQuery(id+"F2.wireOp",EDGE,"E11.2.0.2")])],"isStart":true}),makeQuery(id+"F3.opExtrude","CAP_FACE",FACE,{"disambiguationData":[OSD([subQ0,sQuery(id+"F2.wireOp",EDGE,"E11.3.0.0"),sQuery(id+"F2.wireOp",EDGE,"E11.3.0.1"),sQuery(id+"F2.wireOp",EDGE,"E11.3.0.2")])],"isStart":true}),makeQuery(id+"F3.opExtrude","CAP_FACE",FACE,{"disambiguationData":[OSD([subQ0,sQuery(id+"F2.wireOp",EDGE,"E11.4.0.0"),sQuery(id+"F2.wireOp",EDGE,"E11.4.0.1"),sQuery(id+"F2.wireOp",EDGE,"E11.4.0.2")])],"isStart":true}),makeQuery(id+"F3.opExtrude","CAP_FACE",FACE,{"disambiguationData":[OSD([subQ0,sQuery(id+"F2.wireOp",EDGE,"E11.5.0.0"),sQuery(id+"F2.wireOp",EDGE,"E11.5.0.1"),sQuery(id+"F2.wireOp",EDGE,"E11.5.0.2")])],"isStart":true}),makeQuery(id+"F3.opExtrude","CAP_FACE",FACE,{"disambiguationData":[OSD([subQ0,sQuery(id+"F2.wireOp",EDGE,"E11.6.0.0"),sQuery(id+"F2.wireOp",EDGE,"E11.6.0.1"),sQuery(id+"F2.wireOp",EDGE,"E11.6.0.2")])],"isStart":true}),makeQuery(id+"F3.opExtrude","CAP_FACE",FACE,{"disambiguationData":[OSD([subQ0,sQuery(id+"F2.wireOp",EDGE,"E11.7.0.0"),sQuery(id+"F2.wireOp",EDGE,"E11.7.0.1"),sQuery(id+"F2.wireOp",EDGE,"E11.7.0.2")])],"isStart":true})]})],"blendedInto":[makeQuery(id+"F3.boolean.opBoolean","MERGE",FACE,{"derivedFrom":[makeQuery(id+"F1.opExtrude","SWEPT_FACE",FACE,{"disambiguationData":[OSD([sQuery(id+"F0.wireOp",EDGE,"E0.bottom")])]}),makeQuery(id+"F3.opExtrude","CAP_FACE",FACE,{"disambiguationData":[OSD([subQ0,sQuery(id+"F2.wireOp",EDGE,"E8"),subQ2,subQ1])],"isStart":true}),makeQuery(id+"F3.opExtrude","CAP_FACE",FACE,{"disambiguationData":[OSD([subQ0,sQuery(id+"F2.wireOp",EDGE,"E11.1.0.0"),sQuery(id+"F2.wireOp",EDGE,"E11.1.0.1"),sQuery(id+"F2.wireOp",EDGE,"E11.1.0.2")])],"isStart":true}),makeQuery(id+"F3.opExtrude","CAP_FACE",FACE,{"disambiguationData":[OSD([subQ0,sQuery(id+"F2.wireOp",EDGE,"E11.2.0.0"),sQuery(id+"F2.wireOp",EDGE,"E11.2.0.1"),sQuery(id+"F2.wireOp",EDGE,"E11.2.0.2")])],"isStart":true}),makeQuery(id+"F3.opExtrude","CAP_FACE",FACE,{"disambiguationData":[OSD([subQ0,sQuery(id+"F2.wireOp",EDGE,"E11.3.0.0"),sQuery(id+"F2.wireOp",EDGE,"E11.3.0.1"),sQuery(id+"F2.wireOp",EDGE,"E11.3.0.2")])],"isStart":true}),makeQuery(id+"F3.opExtrude","CAP_FACE",FACE,{"disambiguationData":[OSD([subQ0,sQuery(id+"F2.wireOp",EDGE,"E11.4.0.0"),sQuery(id+"F2.wireOp",EDGE,"E11.4.0.1"),sQuery(id+"F2.wireOp",EDGE,"E11.4.0.2")])],"isStart":true}),makeQuery(id+"F3.opExtrude","CAP_FACE",FACE,{"disambiguationData":[OSD([subQ0,sQuery(id+"F2.wireOp",EDGE,"E11.5.0.0"),sQuery(id+"F2.wireOp",EDGE,"E11.5.0.1"),sQuery(id+"F2.wireOp",EDGE,"E11.5.0.2")])],"isStart":true}),makeQuery(id+"F3.opExtrude","CAP_FACE",FACE,{"disambiguationData":[OSD([subQ0,sQuery(id+"F2.wireOp",EDGE,"E11.6.0.0"),sQuery(id+"F2.wireOp",EDGE,"E11.6.0.1"),sQuery(id+"F2.wireOp",EDGE,"E11.6.0.2")])],"isStart":true}),makeQuery(id+"F3.opExtrude","CAP_FACE",FACE,{"disambiguationData":[OSD([subQ0,sQuery(id+"F2.wireOp",EDGE,"E11.7.0.0"),sQuery(id+"F2.wireOp",EDGE,"E11.7.0.1"),sQuery(id+"F2.wireOp",EDGE,"E11.7.0.2")])],"isStart":true})]})]});}
            var Q9;
            {var subQ0=sQuery(id+"F2.wireOp",EDGE,"E5.0.2");var subQ1=sQuery(id+"F2.wireOp",EDGE,"E11.1.0.2");var subQ2=sQuery(id+"F2.wireOp",EDGE,"E11.1.0.0");Q9=makeQuery(id+"F4.opChamfer","BLEND_EDGE",EDGE,{"blendedFrom":[makeQuery(id+"F3.opExtrude","SWEPT_EDGE",EDGE,{"disambiguationData":[OSD([subQ2,subQ1])]}),makeQuery(id+"F3.boolean.opBoolean","MERGE",FACE,{"derivedFrom":[makeQuery(id+"F1.opExtrude","SWEPT_FACE",FACE,{"disambiguationData":[OSD([sQuery(id+"F0.wireOp",EDGE,"E0.bottom")])]}),makeQuery(id+"F3.opExtrude","CAP_FACE",FACE,{"disambiguationData":[OSD([subQ0,sQuery(id+"F2.wireOp",EDGE,"E8"),sQuery(id+"F2.wireOp",EDGE,"E9"),sQuery(id+"F2.wireOp",EDGE,"E10")])],"isStart":true}),makeQuery(id+"F3.opExtrude","CAP_FACE",FACE,{"disambiguationData":[OSD([subQ0,subQ2,sQuery(id+"F2.wireOp",EDGE,"E11.1.0.1"),subQ1])],"isStart":true}),makeQuery(id+"F3.opExtrude","CAP_FACE",FACE,{"disambiguationData":[OSD([subQ0,sQuery(id+"F2.wireOp",EDGE,"E11.2.0.0"),sQuery(id+"F2.wireOp",EDGE,"E11.2.0.1"),sQuery(id+"F2.wireOp",EDGE,"E11.2.0.2")])],"isStart":true}),makeQuery(id+"F3.opExtrude","CAP_FACE",FACE,{"disambiguationData":[OSD([subQ0,sQuery(id+"F2.wireOp",EDGE,"E11.3.0.0"),sQuery(id+"F2.wireOp",EDGE,"E11.3.0.1"),sQuery(id+"F2.wireOp",EDGE,"E11.3.0.2")])],"isStart":true}),makeQuery(id+"F3.opExtrude","CAP_FACE",FACE,{"disambiguationData":[OSD([subQ0,sQuery(id+"F2.wireOp",EDGE,"E11.4.0.0"),sQuery(id+"F2.wireOp",EDGE,"E11.4.0.1"),sQuery(id+"F2.wireOp",EDGE,"E11.4.0.2")])],"isStart":true}),makeQuery(id+"F3.opExtrude","CAP_FACE",FACE,{"disambiguationData":[OSD([subQ0,sQuery(id+"F2.wireOp",EDGE,"E11.5.0.0"),sQuery(id+"F2.wireOp",EDGE,"E11.5.0.1"),sQuery(id+"F2.wireOp",EDGE,"E11.5.0.2")])],"isStart":true}),makeQuery(id+"F3.opExtrude","CAP_FACE",FACE,{"disambiguationData":[OSD([subQ0,sQuery(id+"F2.wireOp",EDGE,"E11.6.0.0"),sQuery(id+"F2.wireOp",EDGE,"E11.6.0.1"),sQuery(id+"F2.wireOp",EDGE,"E11.6.0.2")])],"isStart":true}),makeQuery(id+"F3.opExtrude","CAP_FACE",FACE,{"disambiguationData":[OSD([subQ0,sQuery(id+"F2.wireOp",EDGE,"E11.7.0.0"),sQuery(id+"F2.wireOp",EDGE,"E11.7.0.1"),sQuery(id+"F2.wireOp",EDGE,"E11.7.0.2")])],"isStart":true})]})],"blendedInto":[makeQuery(id+"F3.boolean.opBoolean","MERGE",FACE,{"derivedFrom":[makeQuery(id+"F1.opExtrude","SWEPT_FACE",FACE,{"disambiguationData":[OSD([sQuery(id+"F0.wireOp",EDGE,"E0.bottom")])]}),makeQuery(id+"F3.opExtrude","CAP_FACE",FACE,{"disambiguationData":[OSD([subQ0,sQuery(id+"F2.wireOp",EDGE,"E8"),sQuery(id+"F2.wireOp",EDGE,"E9"),sQuery(id+"F2.wireOp",EDGE,"E10")])],"isStart":true}),makeQuery(id+"F3.opExtrude","CAP_FACE",FACE,{"disambiguationData":[OSD([subQ0,subQ2,sQuery(id+"F2.wireOp",EDGE,"E11.1.0.1"),subQ1])],"isStart":true}),makeQuery(id+"F3.opExtrude","CAP_FACE",FACE,{"disambiguationData":[OSD([subQ0,sQuery(id+"F2.wireOp",EDGE,"E11.2.0.0"),sQuery(id+"F2.wireOp",EDGE,"E11.2.0.1"),sQuery(id+"F2.wireOp",EDGE,"E11.2.0.2")])],"isStart":true}),makeQuery(id+"F3.opExtrude","CAP_FACE",FACE,{"disambiguationData":[OSD([subQ0,sQuery(id+"F2.wireOp",EDGE,"E11.3.0.0"),sQuery(id+"F2.wireOp",EDGE,"E11.3.0.1"),sQuery(id+"F2.wireOp",EDGE,"E11.3.0.2")])],"isStart":true}),makeQuery(id+"F3.opExtrude","CAP_FACE",FACE,{"disambiguationData":[OSD([subQ0,sQuery(id+"F2.wireOp",EDGE,"E11.4.0.0"),sQuery(id+"F2.wireOp",EDGE,"E11.4.0.1"),sQuery(id+"F2.wireOp",EDGE,"E11.4.0.2")])],"isStart":true}),makeQuery(id+"F3.opExtrude","CAP_FACE",FACE,{"disambiguationData":[OSD([subQ0,sQuery(id+"F2.wireOp",EDGE,"E11.5.0.0"),sQuery(id+"F2.wireOp",EDGE,"E11.5.0.1"),sQuery(id+"F2.wireOp",EDGE,"E11.5.0.2")])],"isStart":true}),makeQuery(id+"F3.opExtrude","CAP_FACE",FACE,{"disambiguationData":[OSD([subQ0,sQuery(id+"F2.wireOp",EDGE,"E11.6.0.0"),sQuery(id+"F2.wireOp",EDGE,"E11.6.0.1"),sQuery(id+"F2.wireOp",EDGE,"E11.6.0.2")])],"isStart":true}),makeQuery(id+"F3.opExtrude","CAP_FACE",FACE,{"disambiguationData":[OSD([subQ0,sQuery(id+"F2.wireOp",EDGE,"E11.7.0.0"),sQuery(id+"F2.wireOp",EDGE,"E11.7.0.1"),sQuery(id+"F2.wireOp",EDGE,"E11.7.0.2")])],"isStart":true})]})]});}
            var Q10;
            {var subQ0=sQuery(id+"F2.wireOp",EDGE,"E5.0.2");var subQ1=sQuery(id+"F2.wireOp",EDGE,"E11.2.0.2");var subQ2=sQuery(id+"F2.wireOp",EDGE,"E11.2.0.0");Q10=makeQuery(id+"F4.opChamfer","BLEND_EDGE",EDGE,{"blendedFrom":[makeQuery(id+"F3.opExtrude","SWEPT_EDGE",EDGE,{"disambiguationData":[OSD([subQ2,subQ1])]}),makeQuery(id+"F3.boolean.opBoolean","MERGE",FACE,{"derivedFrom":[makeQuery(id+"F1.opExtrude","SWEPT_FACE",FACE,{"disambiguationData":[OSD([sQuery(id+"F0.wireOp",EDGE,"E0.bottom")])]}),makeQuery(id+"F3.opExtrude","CAP_FACE",FACE,{"disambiguationData":[OSD([subQ0,sQuery(id+"F2.wireOp",EDGE,"E8"),sQuery(id+"F2.wireOp",EDGE,"E9"),sQuery(id+"F2.wireOp",EDGE,"E10")])],"isStart":true}),makeQuery(id+"F3.opExtrude","CAP_FACE",FACE,{"disambiguationData":[OSD([subQ0,sQuery(id+"F2.wireOp",EDGE,"E11.1.0.0"),sQuery(id+"F2.wireOp",EDGE,"E11.1.0.1"),sQuery(id+"F2.wireOp",EDGE,"E11.1.0.2")])],"isStart":true}),makeQuery(id+"F3.opExtrude","CAP_FACE",FACE,{"disambiguationData":[OSD([subQ0,subQ2,sQuery(id+"F2.wireOp",EDGE,"E11.2.0.1"),subQ1])],"isStart":true}),makeQuery(id+"F3.opExtrude","CAP_FACE",FACE,{"disambiguationData":[OSD([subQ0,sQuery(id+"F2.wireOp",EDGE,"E11.3.0.0"),sQuery(id+"F2.wireOp",EDGE,"E11.3.0.1"),sQuery(id+"F2.wireOp",EDGE,"E11.3.0.2")])],"isStart":true}),makeQuery(id+"F3.opExtrude","CAP_FACE",FACE,{"disambiguationData":[OSD([subQ0,sQuery(id+"F2.wireOp",EDGE,"E11.4.0.0"),sQuery(id+"F2.wireOp",EDGE,"E11.4.0.1"),sQuery(id+"F2.wireOp",EDGE,"E11.4.0.2")])],"isStart":true}),makeQuery(id+"F3.opExtrude","CAP_FACE",FACE,{"disambiguationData":[OSD([subQ0,sQuery(id+"F2.wireOp",EDGE,"E11.5.0.0"),sQuery(id+"F2.wireOp",EDGE,"E11.5.0.1"),sQuery(id+"F2.wireOp",EDGE,"E11.5.0.2")])],"isStart":true}),makeQuery(id+"F3.opExtrude","CAP_FACE",FACE,{"disambiguationData":[OSD([subQ0,sQuery(id+"F2.wireOp",EDGE,"E11.6.0.0"),sQuery(id+"F2.wireOp",EDGE,"E11.6.0.1"),sQuery(id+"F2.wireOp",EDGE,"E11.6.0.2")])],"isStart":true}),makeQuery(id+"F3.opExtrude","CAP_FACE",FACE,{"disambiguationData":[OSD([subQ0,sQuery(id+"F2.wireOp",EDGE,"E11.7.0.0"),sQuery(id+"F2.wireOp",EDGE,"E11.7.0.1"),sQuery(id+"F2.wireOp",EDGE,"E11.7.0.2")])],"isStart":true})]})],"blendedInto":[makeQuery(id+"F3.boolean.opBoolean","MERGE",FACE,{"derivedFrom":[makeQuery(id+"F1.opExtrude","SWEPT_FACE",FACE,{"disambiguationData":[OSD([sQuery(id+"F0.wireOp",EDGE,"E0.bottom")])]}),makeQuery(id+"F3.opExtrude","CAP_FACE",FACE,{"disambiguationData":[OSD([subQ0,sQuery(id+"F2.wireOp",EDGE,"E8"),sQuery(id+"F2.wireOp",EDGE,"E9"),sQuery(id+"F2.wireOp",EDGE,"E10")])],"isStart":true}),makeQuery(id+"F3.opExtrude","CAP_FACE",FACE,{"disambiguationData":[OSD([subQ0,sQuery(id+"F2.wireOp",EDGE,"E11.1.0.0"),sQuery(id+"F2.wireOp",EDGE,"E11.1.0.1"),sQuery(id+"F2.wireOp",EDGE,"E11.1.0.2")])],"isStart":true}),makeQuery(id+"F3.opExtrude","CAP_FACE",FACE,{"disambiguationData":[OSD([subQ0,subQ2,sQuery(id+"F2.wireOp",EDGE,"E11.2.0.1"),subQ1])],"isStart":true}),makeQuery(id+"F3.opExtrude","CAP_FACE",FACE,{"disambiguationData":[OSD([subQ0,sQuery(id+"F2.wireOp",EDGE,"E11.3.0.0"),sQuery(id+"F2.wireOp",EDGE,"E11.3.0.1"),sQuery(id+"F2.wireOp",EDGE,"E11.3.0.2")])],"isStart":true}),makeQuery(id+"F3.opExtrude","CAP_FACE",FACE,{"disambiguationData":[OSD([subQ0,sQuery(id+"F2.wireOp",EDGE,"E11.4.0.0"),sQuery(id+"F2.wireOp",EDGE,"E11.4.0.1"),sQuery(id+"F2.wireOp",EDGE,"E11.4.0.2")])],"isStart":true}),makeQuery(id+"F3.opExtrude","CAP_FACE",FACE,{"disambiguationData":[OSD([subQ0,sQuery(id+"F2.wireOp",EDGE,"E11.5.0.0"),sQuery(id+"F2.wireOp",EDGE,"E11.5.0.1"),sQuery(id+"F2.wireOp",EDGE,"E11.5.0.2")])],"isStart":true}),makeQuery(id+"F3.opExtrude","CAP_FACE",FACE,{"disambiguationData":[OSD([subQ0,sQuery(id+"F2.wireOp",EDGE,"E11.6.0.0"),sQuery(id+"F2.wireOp",EDGE,"E11.6.0.1"),sQuery(id+"F2.wireOp",EDGE,"E11.6.0.2")])],"isStart":true}),makeQuery(id+"F3.opExtrude","CAP_FACE",FACE,{"disambiguationData":[OSD([subQ0,sQuery(id+"F2.wireOp",EDGE,"E11.7.0.0"),sQuery(id+"F2.wireOp",EDGE,"E11.7.0.1"),sQuery(id+"F2.wireOp",EDGE,"E11.7.0.2")])],"isStart":true})]})]});}
            var Q11;
            {var subQ0=sQuery(id+"F2.wireOp",EDGE,"E5.0.2");var subQ1=sQuery(id+"F2.wireOp",EDGE,"E11.3.0.2");var subQ2=sQuery(id+"F2.wireOp",EDGE,"E11.3.0.0");Q11=makeQuery(id+"F4.opChamfer","BLEND_EDGE",EDGE,{"blendedFrom":[makeQuery(id+"F3.opExtrude","SWEPT_EDGE",EDGE,{"disambiguationData":[OSD([subQ2,subQ1])]}),makeQuery(id+"F3.boolean.opBoolean","MERGE",FACE,{"derivedFrom":[makeQuery(id+"F1.opExtrude","SWEPT_FACE",FACE,{"disambiguationData":[OSD([sQuery(id+"F0.wireOp",EDGE,"E0.bottom")])]}),makeQuery(id+"F3.opExtrude","CAP_FACE",FACE,{"disambiguationData":[OSD([subQ0,sQuery(id+"F2.wireOp",EDGE,"E8"),sQuery(id+"F2.wireOp",EDGE,"E9"),sQuery(id+"F2.wireOp",EDGE,"E10")])],"isStart":true}),makeQuery(id+"F3.opExtrude","CAP_FACE",FACE,{"disambiguationData":[OSD([subQ0,sQuery(id+"F2.wireOp",EDGE,"E11.1.0.0"),sQuery(id+"F2.wireOp",EDGE,"E11.1.0.1"),sQuery(id+"F2.wireOp",EDGE,"E11.1.0.2")])],"isStart":true}),makeQuery(id+"F3.opExtrude","CAP_FACE",FACE,{"disambiguationData":[OSD([subQ0,sQuery(id+"F2.wireOp",EDGE,"E11.2.0.0"),sQuery(id+"F2.wireOp",EDGE,"E11.2.0.1"),sQuery(id+"F2.wireOp",EDGE,"E11.2.0.2")])],"isStart":true}),makeQuery(id+"F3.opExtrude","CAP_FACE",FACE,{"disambiguationData":[OSD([subQ0,subQ2,sQuery(id+"F2.wireOp",EDGE,"E11.3.0.1"),subQ1])],"isStart":true}),makeQuery(id+"F3.opExtrude","CAP_FACE",FACE,{"disambiguationData":[OSD([subQ0,sQuery(id+"F2.wireOp",EDGE,"E11.4.0.0"),sQuery(id+"F2.wireOp",EDGE,"E11.4.0.1"),sQuery(id+"F2.wireOp",EDGE,"E11.4.0.2")])],"isStart":true}),makeQuery(id+"F3.opExtrude","CAP_FACE",FACE,{"disambiguationData":[OSD([subQ0,sQuery(id+"F2.wireOp",EDGE,"E11.5.0.0"),sQuery(id+"F2.wireOp",EDGE,"E11.5.0.1"),sQuery(id+"F2.wireOp",EDGE,"E11.5.0.2")])],"isStart":true}),makeQuery(id+"F3.opExtrude","CAP_FACE",FACE,{"disambiguationData":[OSD([subQ0,sQuery(id+"F2.wireOp",EDGE,"E11.6.0.0"),sQuery(id+"F2.wireOp",EDGE,"E11.6.0.1"),sQuery(id+"F2.wireOp",EDGE,"E11.6.0.2")])],"isStart":true}),makeQuery(id+"F3.opExtrude","CAP_FACE",FACE,{"disambiguationData":[OSD([subQ0,sQuery(id+"F2.wireOp",EDGE,"E11.7.0.0"),sQuery(id+"F2.wireOp",EDGE,"E11.7.0.1"),sQuery(id+"F2.wireOp",EDGE,"E11.7.0.2")])],"isStart":true})]})],"blendedInto":[makeQuery(id+"F3.boolean.opBoolean","MERGE",FACE,{"derivedFrom":[makeQuery(id+"F1.opExtrude","SWEPT_FACE",FACE,{"disambiguationData":[OSD([sQuery(id+"F0.wireOp",EDGE,"E0.bottom")])]}),makeQuery(id+"F3.opExtrude","CAP_FACE",FACE,{"disambiguationData":[OSD([subQ0,sQuery(id+"F2.wireOp",EDGE,"E8"),sQuery(id+"F2.wireOp",EDGE,"E9"),sQuery(id+"F2.wireOp",EDGE,"E10")])],"isStart":true}),makeQuery(id+"F3.opExtrude","CAP_FACE",FACE,{"disambiguationData":[OSD([subQ0,sQuery(id+"F2.wireOp",EDGE,"E11.1.0.0"),sQuery(id+"F2.wireOp",EDGE,"E11.1.0.1"),sQuery(id+"F2.wireOp",EDGE,"E11.1.0.2")])],"isStart":true}),makeQuery(id+"F3.opExtrude","CAP_FACE",FACE,{"disambiguationData":[OSD([subQ0,sQuery(id+"F2.wireOp",EDGE,"E11.2.0.0"),sQuery(id+"F2.wireOp",EDGE,"E11.2.0.1"),sQuery(id+"F2.wireOp",EDGE,"E11.2.0.2")])],"isStart":true}),makeQuery(id+"F3.opExtrude","CAP_FACE",FACE,{"disambiguationData":[OSD([subQ0,subQ2,sQuery(id+"F2.wireOp",EDGE,"E11.3.0.1"),subQ1])],"isStart":true}),makeQuery(id+"F3.opExtrude","CAP_FACE",FACE,{"disambiguationData":[OSD([subQ0,sQuery(id+"F2.wireOp",EDGE,"E11.4.0.0"),sQuery(id+"F2.wireOp",EDGE,"E11.4.0.1"),sQuery(id+"F2.wireOp",EDGE,"E11.4.0.2")])],"isStart":true}),makeQuery(id+"F3.opExtrude","CAP_FACE",FACE,{"disambiguationData":[OSD([subQ0,sQuery(id+"F2.wireOp",EDGE,"E11.5.0.0"),sQuery(id+"F2.wireOp",EDGE,"E11.5.0.1"),sQuery(id+"F2.wireOp",EDGE,"E11.5.0.2")])],"isStart":true}),makeQuery(id+"F3.opExtrude","CAP_FACE",FACE,{"disambiguationData":[OSD([subQ0,sQuery(id+"F2.wireOp",EDGE,"E11.6.0.0"),sQuery(id+"F2.wireOp",EDGE,"E11.6.0.1"),sQuery(id+"F2.wireOp",EDGE,"E11.6.0.2")])],"isStart":true}),makeQuery(id+"F3.opExtrude","CAP_FACE",FACE,{"disambiguationData":[OSD([subQ0,sQuery(id+"F2.wireOp",EDGE,"E11.7.0.0"),sQuery(id+"F2.wireOp",EDGE,"E11.7.0.1"),sQuery(id+"F2.wireOp",EDGE,"E11.7.0.2")])],"isStart":true})]})]});}
            var Q12;
            {var subQ0=sQuery(id+"F2.wireOp",EDGE,"E5.0.2");var subQ1=sQuery(id+"F2.wireOp",EDGE,"E11.4.0.2");var subQ2=sQuery(id+"F2.wireOp",EDGE,"E11.4.0.0");Q12=makeQuery(id+"F4.opChamfer","BLEND_EDGE",EDGE,{"blendedFrom":[makeQuery(id+"F3.opExtrude","SWEPT_EDGE",EDGE,{"disambiguationData":[OSD([subQ2,subQ1])]}),makeQuery(id+"F3.boolean.opBoolean","MERGE",FACE,{"derivedFrom":[makeQuery(id+"F1.opExtrude","SWEPT_FACE",FACE,{"disambiguationData":[OSD([sQuery(id+"F0.wireOp",EDGE,"E0.bottom")])]}),makeQuery(id+"F3.opExtrude","CAP_FACE",FACE,{"disambiguationData":[OSD([subQ0,sQuery(id+"F2.wireOp",EDGE,"E8"),sQuery(id+"F2.wireOp",EDGE,"E9"),sQuery(id+"F2.wireOp",EDGE,"E10")])],"isStart":true}),makeQuery(id+"F3.opExtrude","CAP_FACE",FACE,{"disambiguationData":[OSD([subQ0,sQuery(id+"F2.wireOp",EDGE,"E11.1.0.0"),sQuery(id+"F2.wireOp",EDGE,"E11.1.0.1"),sQuery(id+"F2.wireOp",EDGE,"E11.1.0.2")])],"isStart":true}),makeQuery(id+"F3.opExtrude","CAP_FACE",FACE,{"disambiguationData":[OSD([subQ0,sQuery(id+"F2.wireOp",EDGE,"E11.2.0.0"),sQuery(id+"F2.wireOp",EDGE,"E11.2.0.1"),sQuery(id+"F2.wireOp",EDGE,"E11.2.0.2")])],"isStart":true}),makeQuery(id+"F3.opExtrude","CAP_FACE",FACE,{"disambiguationData":[OSD([subQ0,sQuery(id+"F2.wireOp",EDGE,"E11.3.0.0"),sQuery(id+"F2.wireOp",EDGE,"E11.3.0.1"),sQuery(id+"F2.wireOp",EDGE,"E11.3.0.2")])],"isStart":true}),makeQuery(id+"F3.opExtrude","CAP_FACE",FACE,{"disambiguationData":[OSD([subQ0,subQ2,sQuery(id+"F2.wireOp",EDGE,"E11.4.0.1"),subQ1])],"isStart":true}),makeQuery(id+"F3.opExtrude","CAP_FACE",FACE,{"disambiguationData":[OSD([subQ0,sQuery(id+"F2.wireOp",EDGE,"E11.5.0.0"),sQuery(id+"F2.wireOp",EDGE,"E11.5.0.1"),sQuery(id+"F2.wireOp",EDGE,"E11.5.0.2")])],"isStart":true}),makeQuery(id+"F3.opExtrude","CAP_FACE",FACE,{"disambiguationData":[OSD([subQ0,sQuery(id+"F2.wireOp",EDGE,"E11.6.0.0"),sQuery(id+"F2.wireOp",EDGE,"E11.6.0.1"),sQuery(id+"F2.wireOp",EDGE,"E11.6.0.2")])],"isStart":true}),makeQuery(id+"F3.opExtrude","CAP_FACE",FACE,{"disambiguationData":[OSD([subQ0,sQuery(id+"F2.wireOp",EDGE,"E11.7.0.0"),sQuery(id+"F2.wireOp",EDGE,"E11.7.0.1"),sQuery(id+"F2.wireOp",EDGE,"E11.7.0.2")])],"isStart":true})]})],"blendedInto":[makeQuery(id+"F3.boolean.opBoolean","MERGE",FACE,{"derivedFrom":[makeQuery(id+"F1.opExtrude","SWEPT_FACE",FACE,{"disambiguationData":[OSD([sQuery(id+"F0.wireOp",EDGE,"E0.bottom")])]}),makeQuery(id+"F3.opExtrude","CAP_FACE",FACE,{"disambiguationData":[OSD([subQ0,sQuery(id+"F2.wireOp",EDGE,"E8"),sQuery(id+"F2.wireOp",EDGE,"E9"),sQuery(id+"F2.wireOp",EDGE,"E10")])],"isStart":true}),makeQuery(id+"F3.opExtrude","CAP_FACE",FACE,{"disambiguationData":[OSD([subQ0,sQuery(id+"F2.wireOp",EDGE,"E11.1.0.0"),sQuery(id+"F2.wireOp",EDGE,"E11.1.0.1"),sQuery(id+"F2.wireOp",EDGE,"E11.1.0.2")])],"isStart":true}),makeQuery(id+"F3.opExtrude","CAP_FACE",FACE,{"disambiguationData":[OSD([subQ0,sQuery(id+"F2.wireOp",EDGE,"E11.2.0.0"),sQuery(id+"F2.wireOp",EDGE,"E11.2.0.1"),sQuery(id+"F2.wireOp",EDGE,"E11.2.0.2")])],"isStart":true}),makeQuery(id+"F3.opExtrude","CAP_FACE",FACE,{"disambiguationData":[OSD([subQ0,sQuery(id+"F2.wireOp",EDGE,"E11.3.0.0"),sQuery(id+"F2.wireOp",EDGE,"E11.3.0.1"),sQuery(id+"F2.wireOp",EDGE,"E11.3.0.2")])],"isStart":true}),makeQuery(id+"F3.opExtrude","CAP_FACE",FACE,{"disambiguationData":[OSD([subQ0,subQ2,sQuery(id+"F2.wireOp",EDGE,"E11.4.0.1"),subQ1])],"isStart":true}),makeQuery(id+"F3.opExtrude","CAP_FACE",FACE,{"disambiguationData":[OSD([subQ0,sQuery(id+"F2.wireOp",EDGE,"E11.5.0.0"),sQuery(id+"F2.wireOp",EDGE,"E11.5.0.1"),sQuery(id+"F2.wireOp",EDGE,"E11.5.0.2")])],"isStart":true}),makeQuery(id+"F3.opExtrude","CAP_FACE",FACE,{"disambiguationData":[OSD([subQ0,sQuery(id+"F2.wireOp",EDGE,"E11.6.0.0"),sQuery(id+"F2.wireOp",EDGE,"E11.6.0.1"),sQuery(id+"F2.wireOp",EDGE,"E11.6.0.2")])],"isStart":true}),makeQuery(id+"F3.opExtrude","CAP_FACE",FACE,{"disambiguationData":[OSD([subQ0,sQuery(id+"F2.wireOp",EDGE,"E11.7.0.0"),sQuery(id+"F2.wireOp",EDGE,"E11.7.0.1"),sQuery(id+"F2.wireOp",EDGE,"E11.7.0.2")])],"isStart":true})]})]});}
            var Q13;
            {var subQ0=sQuery(id+"F2.wireOp",EDGE,"E5.0.2");var subQ1=sQuery(id+"F2.wireOp",EDGE,"E11.5.0.2");var subQ2=sQuery(id+"F2.wireOp",EDGE,"E11.5.0.0");Q13=makeQuery(id+"F4.opChamfer","BLEND_EDGE",EDGE,{"blendedFrom":[makeQuery(id+"F3.opExtrude","SWEPT_EDGE",EDGE,{"disambiguationData":[OSD([subQ2,subQ1])]}),makeQuery(id+"F3.boolean.opBoolean","MERGE",FACE,{"derivedFrom":[makeQuery(id+"F1.opExtrude","SWEPT_FACE",FACE,{"disambiguationData":[OSD([sQuery(id+"F0.wireOp",EDGE,"E0.bottom")])]}),makeQuery(id+"F3.opExtrude","CAP_FACE",FACE,{"disambiguationData":[OSD([subQ0,sQuery(id+"F2.wireOp",EDGE,"E8"),sQuery(id+"F2.wireOp",EDGE,"E9"),sQuery(id+"F2.wireOp",EDGE,"E10")])],"isStart":true}),makeQuery(id+"F3.opExtrude","CAP_FACE",FACE,{"disambiguationData":[OSD([subQ0,sQuery(id+"F2.wireOp",EDGE,"E11.1.0.0"),sQuery(id+"F2.wireOp",EDGE,"E11.1.0.1"),sQuery(id+"F2.wireOp",EDGE,"E11.1.0.2")])],"isStart":true}),makeQuery(id+"F3.opExtrude","CAP_FACE",FACE,{"disambiguationData":[OSD([subQ0,sQuery(id+"F2.wireOp",EDGE,"E11.2.0.0"),sQuery(id+"F2.wireOp",EDGE,"E11.2.0.1"),sQuery(id+"F2.wireOp",EDGE,"E11.2.0.2")])],"isStart":true}),makeQuery(id+"F3.opExtrude","CAP_FACE",FACE,{"disambiguationData":[OSD([subQ0,sQuery(id+"F2.wireOp",EDGE,"E11.3.0.0"),sQuery(id+"F2.wireOp",EDGE,"E11.3.0.1"),sQuery(id+"F2.wireOp",EDGE,"E11.3.0.2")])],"isStart":true}),makeQuery(id+"F3.opExtrude","CAP_FACE",FACE,{"disambiguationData":[OSD([subQ0,sQuery(id+"F2.wireOp",EDGE,"E11.4.0.0"),sQuery(id+"F2.wireOp",EDGE,"E11.4.0.1"),sQuery(id+"F2.wireOp",EDGE,"E11.4.0.2")])],"isStart":true}),makeQuery(id+"F3.opExtrude","CAP_FACE",FACE,{"disambiguationData":[OSD([subQ0,subQ2,sQuery(id+"F2.wireOp",EDGE,"E11.5.0.1"),subQ1])],"isStart":true}),makeQuery(id+"F3.opExtrude","CAP_FACE",FACE,{"disambiguationData":[OSD([subQ0,sQuery(id+"F2.wireOp",EDGE,"E11.6.0.0"),sQuery(id+"F2.wireOp",EDGE,"E11.6.0.1"),sQuery(id+"F2.wireOp",EDGE,"E11.6.0.2")])],"isStart":true}),makeQuery(id+"F3.opExtrude","CAP_FACE",FACE,{"disambiguationData":[OSD([subQ0,sQuery(id+"F2.wireOp",EDGE,"E11.7.0.0"),sQuery(id+"F2.wireOp",EDGE,"E11.7.0.1"),sQuery(id+"F2.wireOp",EDGE,"E11.7.0.2")])],"isStart":true})]})],"blendedInto":[makeQuery(id+"F3.boolean.opBoolean","MERGE",FACE,{"derivedFrom":[makeQuery(id+"F1.opExtrude","SWEPT_FACE",FACE,{"disambiguationData":[OSD([sQuery(id+"F0.wireOp",EDGE,"E0.bottom")])]}),makeQuery(id+"F3.opExtrude","CAP_FACE",FACE,{"disambiguationData":[OSD([subQ0,sQuery(id+"F2.wireOp",EDGE,"E8"),sQuery(id+"F2.wireOp",EDGE,"E9"),sQuery(id+"F2.wireOp",EDGE,"E10")])],"isStart":true}),makeQuery(id+"F3.opExtrude","CAP_FACE",FACE,{"disambiguationData":[OSD([subQ0,sQuery(id+"F2.wireOp",EDGE,"E11.1.0.0"),sQuery(id+"F2.wireOp",EDGE,"E11.1.0.1"),sQuery(id+"F2.wireOp",EDGE,"E11.1.0.2")])],"isStart":true}),makeQuery(id+"F3.opExtrude","CAP_FACE",FACE,{"disambiguationData":[OSD([subQ0,sQuery(id+"F2.wireOp",EDGE,"E11.2.0.0"),sQuery(id+"F2.wireOp",EDGE,"E11.2.0.1"),sQuery(id+"F2.wireOp",EDGE,"E11.2.0.2")])],"isStart":true}),makeQuery(id+"F3.opExtrude","CAP_FACE",FACE,{"disambiguationData":[OSD([subQ0,sQuery(id+"F2.wireOp",EDGE,"E11.3.0.0"),sQuery(id+"F2.wireOp",EDGE,"E11.3.0.1"),sQuery(id+"F2.wireOp",EDGE,"E11.3.0.2")])],"isStart":true}),makeQuery(id+"F3.opExtrude","CAP_FACE",FACE,{"disambiguationData":[OSD([subQ0,sQuery(id+"F2.wireOp",EDGE,"E11.4.0.0"),sQuery(id+"F2.wireOp",EDGE,"E11.4.0.1"),sQuery(id+"F2.wireOp",EDGE,"E11.4.0.2")])],"isStart":true}),makeQuery(id+"F3.opExtrude","CAP_FACE",FACE,{"disambiguationData":[OSD([subQ0,subQ2,sQuery(id+"F2.wireOp",EDGE,"E11.5.0.1"),subQ1])],"isStart":true}),makeQuery(id+"F3.opExtrude","CAP_FACE",FACE,{"disambiguationData":[OSD([subQ0,sQuery(id+"F2.wireOp",EDGE,"E11.6.0.0"),sQuery(id+"F2.wireOp",EDGE,"E11.6.0.1"),sQuery(id+"F2.wireOp",EDGE,"E11.6.0.2")])],"isStart":true}),makeQuery(id+"F3.opExtrude","CAP_FACE",FACE,{"disambiguationData":[OSD([subQ0,sQuery(id+"F2.wireOp",EDGE,"E11.7.0.0"),sQuery(id+"F2.wireOp",EDGE,"E11.7.0.1"),sQuery(id+"F2.wireOp",EDGE,"E11.7.0.2")])],"isStart":true})]})]});}
            var Q14;
            {var subQ0=sQuery(id+"F2.wireOp",EDGE,"E5.0.2");var subQ1=sQuery(id+"F2.wireOp",EDGE,"E11.6.0.2");var subQ2=sQuery(id+"F2.wireOp",EDGE,"E11.6.0.0");Q14=makeQuery(id+"F4.opChamfer","BLEND_EDGE",EDGE,{"blendedFrom":[makeQuery(id+"F3.opExtrude","SWEPT_EDGE",EDGE,{"disambiguationData":[OSD([subQ2,subQ1])]}),makeQuery(id+"F3.boolean.opBoolean","MERGE",FACE,{"derivedFrom":[makeQuery(id+"F1.opExtrude","SWEPT_FACE",FACE,{"disambiguationData":[OSD([sQuery(id+"F0.wireOp",EDGE,"E0.bottom")])]}),makeQuery(id+"F3.opExtrude","CAP_FACE",FACE,{"disambiguationData":[OSD([subQ0,sQuery(id+"F2.wireOp",EDGE,"E8"),sQuery(id+"F2.wireOp",EDGE,"E9"),sQuery(id+"F2.wireOp",EDGE,"E10")])],"isStart":true}),makeQuery(id+"F3.opExtrude","CAP_FACE",FACE,{"disambiguationData":[OSD([subQ0,sQuery(id+"F2.wireOp",EDGE,"E11.1.0.0"),sQuery(id+"F2.wireOp",EDGE,"E11.1.0.1"),sQuery(id+"F2.wireOp",EDGE,"E11.1.0.2")])],"isStart":true}),makeQuery(id+"F3.opExtrude","CAP_FACE",FACE,{"disambiguationData":[OSD([subQ0,sQuery(id+"F2.wireOp",EDGE,"E11.2.0.0"),sQuery(id+"F2.wireOp",EDGE,"E11.2.0.1"),sQuery(id+"F2.wireOp",EDGE,"E11.2.0.2")])],"isStart":true}),makeQuery(id+"F3.opExtrude","CAP_FACE",FACE,{"disambiguationData":[OSD([subQ0,sQuery(id+"F2.wireOp",EDGE,"E11.3.0.0"),sQuery(id+"F2.wireOp",EDGE,"E11.3.0.1"),sQuery(id+"F2.wireOp",EDGE,"E11.3.0.2")])],"isStart":true}),makeQuery(id+"F3.opExtrude","CAP_FACE",FACE,{"disambiguationData":[OSD([subQ0,sQuery(id+"F2.wireOp",EDGE,"E11.4.0.0"),sQuery(id+"F2.wireOp",EDGE,"E11.4.0.1"),sQuery(id+"F2.wireOp",EDGE,"E11.4.0.2")])],"isStart":true}),makeQuery(id+"F3.opExtrude","CAP_FACE",FACE,{"disambiguationData":[OSD([subQ0,sQuery(id+"F2.wireOp",EDGE,"E11.5.0.0"),sQuery(id+"F2.wireOp",EDGE,"E11.5.0.1"),sQuery(id+"F2.wireOp",EDGE,"E11.5.0.2")])],"isStart":true}),makeQuery(id+"F3.opExtrude","CAP_FACE",FACE,{"disambiguationData":[OSD([subQ0,subQ2,sQuery(id+"F2.wireOp",EDGE,"E11.6.0.1"),subQ1])],"isStart":true}),makeQuery(id+"F3.opExtrude","CAP_FACE",FACE,{"disambiguationData":[OSD([subQ0,sQuery(id+"F2.wireOp",EDGE,"E11.7.0.0"),sQuery(id+"F2.wireOp",EDGE,"E11.7.0.1"),sQuery(id+"F2.wireOp",EDGE,"E11.7.0.2")])],"isStart":true})]})],"blendedInto":[makeQuery(id+"F3.boolean.opBoolean","MERGE",FACE,{"derivedFrom":[makeQuery(id+"F1.opExtrude","SWEPT_FACE",FACE,{"disambiguationData":[OSD([sQuery(id+"F0.wireOp",EDGE,"E0.bottom")])]}),makeQuery(id+"F3.opExtrude","CAP_FACE",FACE,{"disambiguationData":[OSD([subQ0,sQuery(id+"F2.wireOp",EDGE,"E8"),sQuery(id+"F2.wireOp",EDGE,"E9"),sQuery(id+"F2.wireOp",EDGE,"E10")])],"isStart":true}),makeQuery(id+"F3.opExtrude","CAP_FACE",FACE,{"disambiguationData":[OSD([subQ0,sQuery(id+"F2.wireOp",EDGE,"E11.1.0.0"),sQuery(id+"F2.wireOp",EDGE,"E11.1.0.1"),sQuery(id+"F2.wireOp",EDGE,"E11.1.0.2")])],"isStart":true}),makeQuery(id+"F3.opExtrude","CAP_FACE",FACE,{"disambiguationData":[OSD([subQ0,sQuery(id+"F2.wireOp",EDGE,"E11.2.0.0"),sQuery(id+"F2.wireOp",EDGE,"E11.2.0.1"),sQuery(id+"F2.wireOp",EDGE,"E11.2.0.2")])],"isStart":true}),makeQuery(id+"F3.opExtrude","CAP_FACE",FACE,{"disambiguationData":[OSD([subQ0,sQuery(id+"F2.wireOp",EDGE,"E11.3.0.0"),sQuery(id+"F2.wireOp",EDGE,"E11.3.0.1"),sQuery(id+"F2.wireOp",EDGE,"E11.3.0.2")])],"isStart":true}),makeQuery(id+"F3.opExtrude","CAP_FACE",FACE,{"disambiguationData":[OSD([subQ0,sQuery(id+"F2.wireOp",EDGE,"E11.4.0.0"),sQuery(id+"F2.wireOp",EDGE,"E11.4.0.1"),sQuery(id+"F2.wireOp",EDGE,"E11.4.0.2")])],"isStart":true}),makeQuery(id+"F3.opExtrude","CAP_FACE",FACE,{"disambiguationData":[OSD([subQ0,sQuery(id+"F2.wireOp",EDGE,"E11.5.0.0"),sQuery(id+"F2.wireOp",EDGE,"E11.5.0.1"),sQuery(id+"F2.wireOp",EDGE,"E11.5.0.2")])],"isStart":true}),makeQuery(id+"F3.opExtrude","CAP_FACE",FACE,{"disambiguationData":[OSD([subQ0,subQ2,sQuery(id+"F2.wireOp",EDGE,"E11.6.0.1"),subQ1])],"isStart":true}),makeQuery(id+"F3.opExtrude","CAP_FACE",FACE,{"disambiguationData":[OSD([subQ0,sQuery(id+"F2.wireOp",EDGE,"E11.7.0.0"),sQuery(id+"F2.wireOp",EDGE,"E11.7.0.1"),sQuery(id+"F2.wireOp",EDGE,"E11.7.0.2")])],"isStart":true})]})]});}
            var Q15;
            {var subQ0=sQuery(id+"F2.wireOp",EDGE,"E11.7.0.2");var subQ1=sQuery(id+"F2.wireOp",EDGE,"E11.7.0.0");var subQ2=sQuery(id+"F2.wireOp",EDGE,"E5.0.2");Q15=makeQuery(id+"F4.opChamfer","BLEND_EDGE",EDGE,{"blendedFrom":[makeQuery(id+"F3.opExtrude","SWEPT_EDGE",EDGE,{"disambiguationData":[OSD([subQ1,subQ0])]}),makeQuery(id+"F3.boolean.opBoolean","MERGE",FACE,{"derivedFrom":[makeQuery(id+"F1.opExtrude","SWEPT_FACE",FACE,{"disambiguationData":[OSD([sQuery(id+"F0.wireOp",EDGE,"E0.bottom")])]}),makeQuery(id+"F3.opExtrude","CAP_FACE",FACE,{"disambiguationData":[OSD([subQ2,sQuery(id+"F2.wireOp",EDGE,"E8"),sQuery(id+"F2.wireOp",EDGE,"E9"),sQuery(id+"F2.wireOp",EDGE,"E10")])],"isStart":true}),makeQuery(id+"F3.opExtrude","CAP_FACE",FACE,{"disambiguationData":[OSD([subQ2,sQuery(id+"F2.wireOp",EDGE,"E11.1.0.0"),sQuery(id+"F2.wireOp",EDGE,"E11.1.0.1"),sQuery(id+"F2.wireOp",EDGE,"E11.1.0.2")])],"isStart":true}),makeQuery(id+"F3.opExtrude","CAP_FACE",FACE,{"disambiguationData":[OSD([subQ2,sQuery(id+"F2.wireOp",EDGE,"E11.2.0.0"),sQuery(id+"F2.wireOp",EDGE,"E11.2.0.1"),sQuery(id+"F2.wireOp",EDGE,"E11.2.0.2")])],"isStart":true}),makeQuery(id+"F3.opExtrude","CAP_FACE",FACE,{"disambiguationData":[OSD([subQ2,sQuery(id+"F2.wireOp",EDGE,"E11.3.0.0"),sQuery(id+"F2.wireOp",EDGE,"E11.3.0.1"),sQuery(id+"F2.wireOp",EDGE,"E11.3.0.2")])],"isStart":true}),makeQuery(id+"F3.opExtrude","CAP_FACE",FACE,{"disambiguationData":[OSD([subQ2,sQuery(id+"F2.wireOp",EDGE,"E11.4.0.0"),sQuery(id+"F2.wireOp",EDGE,"E11.4.0.1"),sQuery(id+"F2.wireOp",EDGE,"E11.4.0.2")])],"isStart":true}),makeQuery(id+"F3.opExtrude","CAP_FACE",FACE,{"disambiguationData":[OSD([subQ2,sQuery(id+"F2.wireOp",EDGE,"E11.5.0.0"),sQuery(id+"F2.wireOp",EDGE,"E11.5.0.1"),sQuery(id+"F2.wireOp",EDGE,"E11.5.0.2")])],"isStart":true}),makeQuery(id+"F3.opExtrude","CAP_FACE",FACE,{"disambiguationData":[OSD([subQ2,sQuery(id+"F2.wireOp",EDGE,"E11.6.0.0"),sQuery(id+"F2.wireOp",EDGE,"E11.6.0.1"),sQuery(id+"F2.wireOp",EDGE,"E11.6.0.2")])],"isStart":true}),makeQuery(id+"F3.opExtrude","CAP_FACE",FACE,{"disambiguationData":[OSD([subQ2,subQ1,sQuery(id+"F2.wireOp",EDGE,"E11.7.0.1"),subQ0])],"isStart":true})]})],"blendedInto":[makeQuery(id+"F3.boolean.opBoolean","MERGE",FACE,{"derivedFrom":[makeQuery(id+"F1.opExtrude","SWEPT_FACE",FACE,{"disambiguationData":[OSD([sQuery(id+"F0.wireOp",EDGE,"E0.bottom")])]}),makeQuery(id+"F3.opExtrude","CAP_FACE",FACE,{"disambiguationData":[OSD([subQ2,sQuery(id+"F2.wireOp",EDGE,"E8"),sQuery(id+"F2.wireOp",EDGE,"E9"),sQuery(id+"F2.wireOp",EDGE,"E10")])],"isStart":true}),makeQuery(id+"F3.opExtrude","CAP_FACE",FACE,{"disambiguationData":[OSD([subQ2,sQuery(id+"F2.wireOp",EDGE,"E11.1.0.0"),sQuery(id+"F2.wireOp",EDGE,"E11.1.0.1"),sQuery(id+"F2.wireOp",EDGE,"E11.1.0.2")])],"isStart":true}),makeQuery(id+"F3.opExtrude","CAP_FACE",FACE,{"disambiguationData":[OSD([subQ2,sQuery(id+"F2.wireOp",EDGE,"E11.2.0.0"),sQuery(id+"F2.wireOp",EDGE,"E11.2.0.1"),sQuery(id+"F2.wireOp",EDGE,"E11.2.0.2")])],"isStart":true}),makeQuery(id+"F3.opExtrude","CAP_FACE",FACE,{"disambiguationData":[OSD([subQ2,sQuery(id+"F2.wireOp",EDGE,"E11.3.0.0"),sQuery(id+"F2.wireOp",EDGE,"E11.3.0.1"),sQuery(id+"F2.wireOp",EDGE,"E11.3.0.2")])],"isStart":true}),makeQuery(id+"F3.opExtrude","CAP_FACE",FACE,{"disambiguationData":[OSD([subQ2,sQuery(id+"F2.wireOp",EDGE,"E11.4.0.0"),sQuery(id+"F2.wireOp",EDGE,"E11.4.0.1"),sQuery(id+"F2.wireOp",EDGE,"E11.4.0.2")])],"isStart":true}),makeQuery(id+"F3.opExtrude","CAP_FACE",FACE,{"disambiguationData":[OSD([subQ2,sQuery(id+"F2.wireOp",EDGE,"E11.5.0.0"),sQuery(id+"F2.wireOp",EDGE,"E11.5.0.1"),sQuery(id+"F2.wireOp",EDGE,"E11.5.0.2")])],"isStart":true}),makeQuery(id+"F3.opExtrude","CAP_FACE",FACE,{"disambiguationData":[OSD([subQ2,sQuery(id+"F2.wireOp",EDGE,"E11.6.0.0"),sQuery(id+"F2.wireOp",EDGE,"E11.6.0.1"),sQuery(id+"F2.wireOp",EDGE,"E11.6.0.2")])],"isStart":true}),makeQuery(id+"F3.opExtrude","CAP_FACE",FACE,{"disambiguationData":[OSD([subQ2,subQ1,sQuery(id+"F2.wireOp",EDGE,"E11.7.0.1"),subQ0])],"isStart":true})]})]});}
            fillet(context, id + "F5", {"entities" : qUnion([Q0, Q1, Q2, Q3, Q4, Q5, Q6, Q7, Q8, Q9, Q10, Q11, Q12, Q13, Q14, Q15]), "radius" : 2 * mm, "tangentPropagation" : true, "allowEdgeOverflow" : false});
        }
    });
